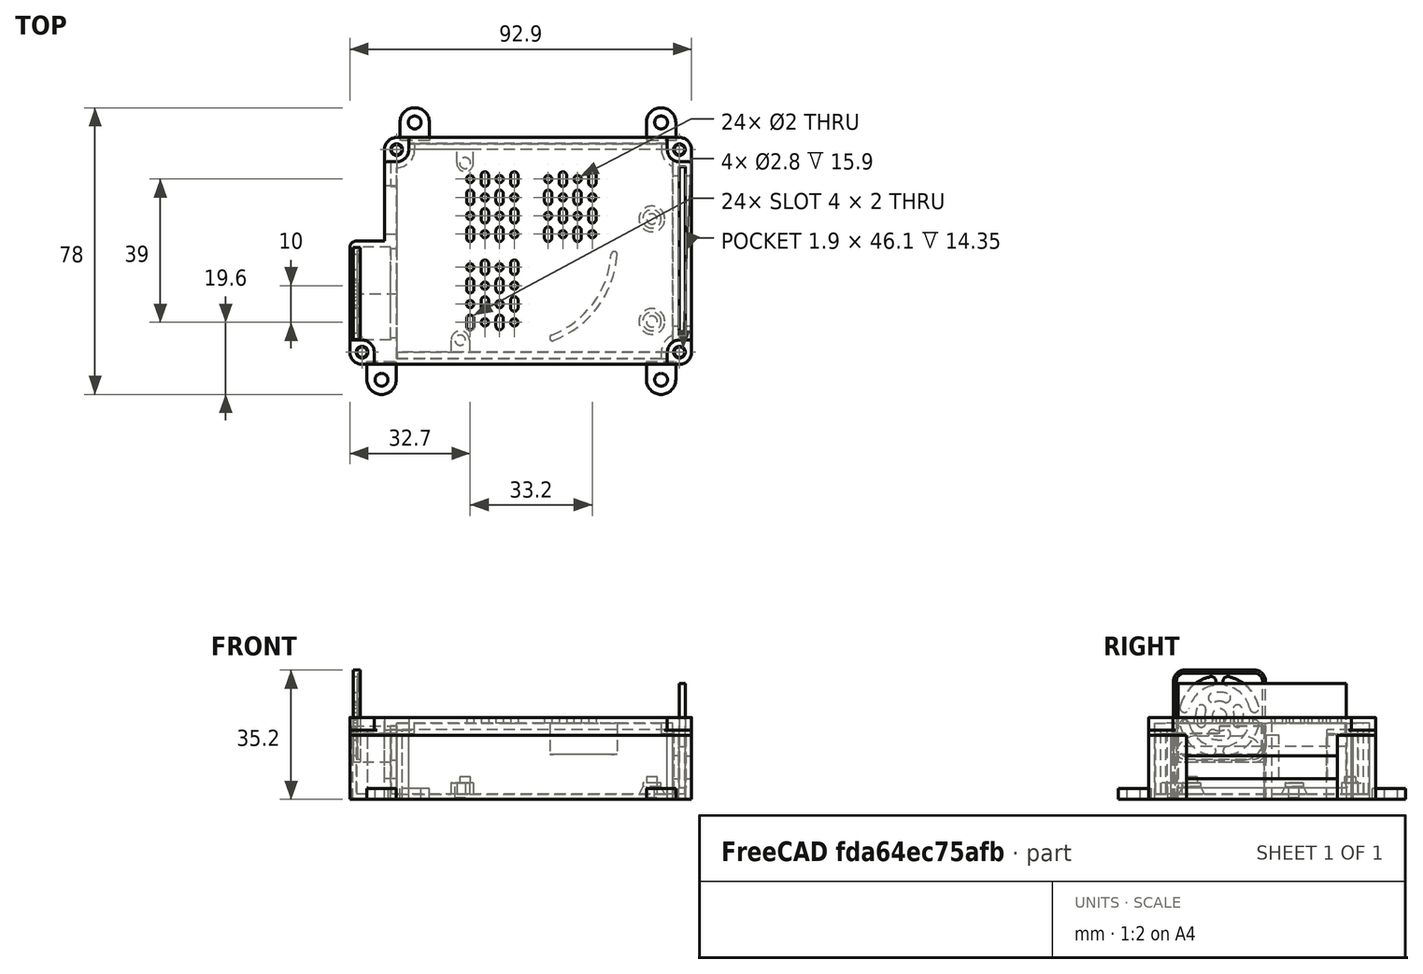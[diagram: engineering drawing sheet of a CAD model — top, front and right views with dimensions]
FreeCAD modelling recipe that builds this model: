
FCSTD DOCUMENT  (FreeCAD 1.0R39319 (Git))
Label: Enclosure
License: All rights reserved
LicenseURL: https://en.wikipedia.org/wiki/All_rights_reserved
objects: Sketcher::SketchObject×31, PartDesign::Pocket×17, PartDesign::Pad×13, PartDesign::Body×9, PartDesign::Fillet×8, PartDesign::FeatureBase×4, App::Part×3, Mesh::Feature×2, PartDesign::PolarPattern×2, Spreadsheet::Sheet×1, PartDesign::Chamfer×1
note: 200 computed .brp shape members not serialized (recipe doc carries the construction recipe); baked Part::Feature solids carry a one-line shape summary decoded from their .brp

FEATURE [Sketcher::SketchObject] Sketch  label="Bottom_base_sketch"
  ArcFitTolerance = 1e-06
  AttachmentSupport = -> [XY_Plane]
  FullyConstrained = true
  MakeInternals = false
  MapMode = 5
  expr: .Constraints.Fan_lower_wall_distance = (Spreadsheet.B1 * 2 + 0.1 mm) * 2
  expr: Constraints[53] = Spreadsheet.B1 * 2
  expr: Constraints[54] = Spreadsheet.B1 * 2
  expr: Constraints[56] = Spreadsheet.B1
  expr: Constraints[57] = Spreadsheet.B1 / 2
  expr: Constraints[58] = Spreadsheet.B1 * 2 + 4 mm
  expr: Constraints[67] = Spreadsheet.B1 + 0.1 mm
  sketch-geometry (20):
    g0: LineSegment [constr] StartX=20 StartY=73.3 StartZ=0 EndX=20 EndY=20 EndZ=0
    g1: LineSegment [constr] StartX=20 StartY=20 StartZ=0 EndX=88.6 EndY=20 EndZ=0
    g2: LineSegment [constr] StartX=86 StartY=73.3 StartZ=0 EndX=20 EndY=73.3 EndZ=0
    g3: LineSegment [constr] StartX=86 StartY=73.3 StartZ=0 EndX=86 EndY=60.5 EndZ=0
    g4: LineSegment [constr] StartX=86 StartY=60.5 StartZ=0 EndX=88.6 EndY=60.5 EndZ=0
    g5: LineSegment [constr] StartX=88.6 StartY=60.5 StartZ=0 EndX=88.6 EndY=20 EndZ=0
    g6: LineSegment [constr] StartX=19 StartY=74.3 StartZ=0 EndX=19 EndY=19 EndZ=0
    g7: LineSegment [constr] StartX=19 StartY=19 StartZ=0 EndX=89.6 EndY=19 EndZ=0
    g8: LineSegment [constr] StartX=89.6 StartY=19 StartZ=0 EndX=89.6 EndY=74.3 EndZ=0
    g9: LineSegment [constr] StartX=89.6 StartY=74.3 StartZ=0 EndX=19 EndY=74.3 EndZ=0
    g10: LineSegment [constr] StartX=4.7 StartY=47.7 StartZ=0 EndX=4.7 EndY=22.4 EndZ=0
    g11: LineSegment [constr] StartX=4.7 StartY=22.4 StartZ=0 EndX=15 EndY=22.4 EndZ=0
    g12: LineSegment [constr] StartX=15 StartY=22.4 StartZ=0 EndX=15 EndY=47.7 EndZ=0
    g13: LineSegment [constr] StartX=15 StartY=47.7 StartZ=0 EndX=4.7 EndY=47.7 EndZ=0
    g14: LineSegment StartX=13.3 StartY=49.3 StartZ=0 EndX=13.3 EndY=77.5 EndZ=0
    g15: LineSegment StartX=13.3 StartY=77.5 StartZ=0 EndX=96.8 EndY=77.5 EndZ=0
    g16: LineSegment StartX=96.8 StartY=77.5 StartZ=0 EndX=96.8 EndY=15.8 EndZ=0
    g17: LineSegment StartX=96.8 StartY=15.8 StartZ=0 EndX=3.9 EndY=15.8 EndZ=0
    g18: LineSegment StartX=3.9 StartY=15.8 StartZ=0 EndX=3.9 EndY=49.3 EndZ=0
    g19: LineSegment StartX=3.9 StartY=49.3 StartZ=0 EndX=13.3 EndY=49.3 EndZ=0
  constraints (68):
    c: Vertical(g0)
    c: Horizontal(g1)
    c: Horizontal(g2)
    c: Distance(g0) = 53.3  'PCB_height'
    c: DistanceY(g-1,g0) = 20  'Offset'
    c: DistanceX(g-2,g0) = 20
    c: Distance(g1) = 68.6
    c: Coincident(g1,g0)
    c: Coincident(g2,g0)
    c: Coincident(g3,g2)
    c: Vertical(g3)
    c: Coincident(g4,g3)
    c: Horizontal(g4)
    c: Coincident(g5,g4)
    c: Coincident(g5,g1)
    c: Vertical(g5)
    c: Distance(g2) = 66  'Short_length'
    c: Distance(g3) = 12.8
    c: Coincident(g6,g7)
    c: Coincident(g7,g8)
    c: Coincident(g8,g9)
    c: Coincident(g9,g6)
    c: Vertical(g6)
    c: Vertical(g8)
    c: Horizontal(g7)
    c: Horizontal(g9)
    c: DistanceX(g6,g0) = 1
    c: DistanceY(g2,g8) = 1
    c: DistanceX(g1,g7) = 1
    c: DistanceY(g6,g0) = 1
    c: Coincident(g10,g11)
    c: Coincident(g11,g12)
    c: Coincident(g12,g13)
    c: Coincident(g13,g10)
    c: Vertical(g10)
    c: Vertical(g12)
    c: Horizontal(g11)
    c: Horizontal(g13)
    c: Distance(g10) = 25.3  'Fan_height'
    c: Distance(g11) = 10.3  'Fan_width'
    c: Distance(g11,g0) = 5  'Fan_board_distance'
    c: Vertical(g14)
    c: Coincident(g15,g14)
    c: Horizontal(g15)
    c: Coincident(g16,g15)
    c: Vertical(g16)
    c: Coincident(g17,g16)
    c: Horizontal(g17)
    c: Coincident(g18,g17)
    c: Vertical(g18)
    c: Coincident(g19,g18)
    c: Coincident(g19,g14)
    c: Horizontal(g19)
    c: Distance(g6,g15) = 3.2
    c: Distance(g7,g17) = 3.2
    c: Distance(g14,g0) = 6.7
    c: Distance(g14,g13) = 1.6
    c: Distance(g18,g10) = 0.8
    c: Distance(g16,g8) = 7.2
    c: DistanceX(g-2,g17) = 3.9  'Outer_leftmost_distance'
    c: DistanceY(g-1,g17) = 15.8  'Outer_downmost_distance'
    c: Distance(g19) = 9.4  'Fan_housing_h_length'
    c: Distance(g17) = 92.9  'Outer_housing_width'
    c: Distance(g18) = 33.5  'Fan_housing_v_length'
    c: Distance(g16) = 61.7  'Outer_housing_height'
    c: Distance(g11,g17) = 6.6  'Fan_lower_wall_distance'
    c: DistanceY(g0,g11) = 2.4  'Fan_board_verical_offset'
    c: Distance(g12,g14) = 1.7
FEATURE [Spreadsheet::Sheet] Spreadsheet
  cells = A1='Wall thickness; B1==1.6 mm; A2='Bottom thickness; B2==1.5 mm; A3='USB connector width; B3==13.1 mm; A4='USB connector edge distance; B4==31.2 mm; A5='Top thickness; B5==1.5 mm
FEATURE [PartDesign::Pad] Pad  label="Bottom_base"
  Direction = (0,0,1)
  Length = 1.5
  Length2 = 10
  Profile = -> Sketch
  ReferenceAxis = -> Sketch [N_Axis]
  Refine = true
  Suppressed = false
  Type = 0
  expr: Length = Spreadsheet.B2
FEATURE [Sketcher::SketchObject] Sketch001  label="Bottom_outer_wall_sketch"
  ArcFitTolerance = 1e-06
  AttachmentSupport = -> [Pad]
  FullyConstrained = true
  MakeInternals = false
  MapMode = 5
  Placement = pos=(0,0,1.5) rot=(0,0,1;0rad)
  expr: .Constraints.Breakout_wall_thickness = Spreadsheet.B1 * 2 + 1.9 mm
  expr: .Constraints.Wall_thickness = Spreadsheet.B1 * 2 + 0.1 mm
  expr: Constraints[12] = <<Bottom_base_sketch>>.Constraints.Outer_leftmost_distance
  expr: Constraints[13] = <<Bottom_base_sketch>>.Constraints.Fan_housing_v_length
  expr: Constraints[14] = <<Bottom_base_sketch>>.Constraints.Outer_downmost_distance
  expr: Constraints[15] = <<Bottom_base_sketch>>.Constraints.Outer_housing_width
  expr: Constraints[16] = <<Bottom_base_sketch>>.Constraints.Outer_housing_height
  expr: Constraints[17] = <<Bottom_base_sketch>>.Constraints.Fan_housing_h_length
  expr: Constraints[18] = .Constraints.Wall_thickness
  expr: Constraints[19] = <<Bottom_base_sketch>>.Constraints.Offset
  expr: Constraints[20] = <<Bottom_base_sketch>>.Constraints.Offset
  expr: Constraints[27] = <<Bottom_base_sketch>>.Constraints.Fan_height
  expr: Constraints[32] = .Constraints.Wall_thickness
  expr: Constraints[37] = .Constraints.Wall_thickness
  expr: Constraints[38] = .Constraints.Wall_thickness
  expr: Constraints[44] = .Constraints.Wall_thickness
  expr: Constraints[59] = <<Bottom_base_sketch>>.Constraints.Fan_board_distance
  expr: Constraints[60] = <<Bottom_base_sketch>>.Constraints.Fan_board_verical_offset
  expr: Constraints[63] = .Constraints.Wall_thickness
  sketch-geometry (19):
    g0: LineSegment StartX=96.8 StartY=77.5 StartZ=0 EndX=13.3 EndY=77.5 EndZ=0
    g1: LineSegment StartX=13.3 StartY=77.5 StartZ=0 EndX=13.3 EndY=49.3 EndZ=0
    g2: LineSegment StartX=13.3 StartY=49.3 StartZ=0 EndX=3.9 EndY=49.3 EndZ=0
    g3: LineSegment StartX=3.9 StartY=49.3 StartZ=0 EndX=3.9 EndY=15.8 EndZ=0
    g4: LineSegment StartX=3.9 StartY=15.8 StartZ=0 EndX=96.8 EndY=15.8 EndZ=0
    g5: LineSegment StartX=96.8 StartY=15.8 StartZ=0 EndX=96.8 EndY=77.5 EndZ=0
    g6: GeomPoint [constr] X=20 Y=20 Z=0
    g7: LineSegment [constr] StartX=4.7 StartY=47.7 StartZ=0 EndX=4.7 EndY=22.4 EndZ=0
    g8: LineSegment [constr] StartX=15 StartY=22.4 StartZ=0 EndX=15 EndY=47.7 EndZ=0
    g9: LineSegment [constr] StartX=15 StartY=47.7 StartZ=0 EndX=4.7 EndY=47.7 EndZ=0
    g10: LineSegment StartX=16.6 StartY=70.9 StartZ=0 EndX=16.6 EndY=19.1 EndZ=0
    g11: ArcOfCircle CenterX=16.6 CenterY=74.2 CenterZ=0 NormalX=0 NormalY=0 NormalZ=1 AngleXU=0 Radius=3.3 StartAngle=4.71239 EndAngle=6.28319
    g12: LineSegment StartX=90.2 StartY=74.2 StartZ=0 EndX=19.9 EndY=74.2 EndZ=0
    g13: ArcOfCircle CenterX=93.5 CenterY=74.2 CenterZ=0 NormalX=0 NormalY=0 NormalZ=1 AngleXU=0 Radius=3.3 StartAngle=3.14159 EndAngle=4.13546
    g14: LineSegment StartX=91.7 StartY=21.8659 StartZ=0 EndX=91.7 EndY=71.4341 EndZ=0
    g15: LineSegment StartX=16.6 StartY=19.1 StartZ=0 EndX=90.2 EndY=19.1 EndZ=0
    g16: ArcOfCircle CenterX=93.5 CenterY=19.1 CenterZ=0 NormalX=0 NormalY=0 NormalZ=1 AngleXU=0 Radius=3.3 StartAngle=2.14773 EndAngle=3.14159
    g17: LineSegment [constr] StartX=4.7 StartY=22.4 StartZ=0 EndX=15 EndY=22.4 EndZ=0
    g18: LineSegment [constr] StartX=93.5 StartY=19.1 StartZ=0 EndX=93.5 EndY=74.2 EndZ=0
  constraints (68):
    c: Horizontal(g0)
    c: Coincident(g1,g0)
    c: Vertical(g1)
    c: Coincident(g2,g1)
    c: Horizontal(g2)
    c: Coincident(g3,g2)
    c: Vertical(g3)
    c: Coincident(g4,g3)
    c: Horizontal(g4)
    c: Coincident(g5,g4)
    c: Coincident(g5,g0)
    c: Vertical(g5)
    c: DistanceX(g-2,g3) = 3.9
    c: Distance(g3) = 33.5
    c: DistanceY(g-1,g3) = 15.8
    c: Distance(g4) = 92.9
    c: Distance(g5) = 61.7
    c: Distance(g2) = 9.4
    c: DistanceY(g3,g15) = 3.3
    c: DistanceX(g-2,g6) = 20
    c: DistanceY(g-1,g6) = 20
    c: Coincident(g7,g17)
    c: Coincident(g8,g9)
    c: Coincident(g9,g7)
    c: Vertical(g7)
    c: Vertical(g8)
    c: Horizontal(g9)
    c: Distance(g7) = 25.3
    c: Vertical(g10)
    c: Distance(g10,g1) = 3.3  'Wall_thickness'
    c: Coincident(g11,g12)
    c: Coincident(g11,g10)
    c: Radius(g11) = 3.3
    c: PointOnObject(g11,g10)
    c: Horizontal(g12)
    c: Coincident(g13,g12)
    c: Coincident(g13,g14)
    c: Radius(g13) = 3.3
    c: Distance(g13,g0) = 3.3
    c: PointOnObject(g11,g12)
    c: Vertical(g14)
    c: Horizontal(g15)
    c: Coincident(g16,g14)
    c: Coincident(g16,g15)
    c: Radius(g16) = 3.3
    c: Distance(g14,g5) = 5.1  'Breakout_wall_thickness'
    c: Distance(g-1,g10) = 16.6  'Left_inner_wall_distance'
    c: Distance(g-1,g15) = 19.1  'Lower_inner_wall_distance'
    c: Distance(g-1,g12) = 74.2  'Upper_inner_wall_distance'
    c: Distance(g12) = 70.3  'Uppoer_pos_pin_length'
    c: Distance(g15) = 73.6  'Lower_pos_pin_length'
    c: Distance(g6,g14) = 71.7  'Breakout_board_distance'
    c: DistanceX(g-2,g11) = 16.6  'Left_hole_h_distance'
    c: DistanceY(g-1,g11) = 74.2  'Upper_hole_h_distance'
    c: DistanceY(g-1,g16) = 19.1  'Lower_hole_h_distance'
    c: DistanceX(g-2,g16) = 93.5  'Right_hole_h_distance'
    c: Horizontal(g17)
    c: Distance(g17,g8) = 10.3
    c: Coincident(g17,g8)
    c: DistanceX(g8,g6) = 5
    c: DistanceY(g6,g8) = 2.4
    c: PointOnObject(g16,g15)
    c: PointOnObject(g13,g12)
    c: Distance(g13,g5) = 3.3
    c: Coincident(g18,g16)
    c: Coincident(g18,g13)
    c: Vertical(g18)
    c: Coincident(g10,g15)
FEATURE [PartDesign::Pad] Pad001  label="Bottom_outer_wall"
  BaseFeature = -> Pad
  Direction = (0,0,1)
  Length = 15.9
  Length2 = 10
  Profile = -> Sketch001
  ReferenceAxis = -> Sketch001 [N_Axis]
  Refine = true
  Suppressed = false
  Type = 0
  expr: Length = 15.9 mm
FEATURE [Mesh::Feature] Fan
  Placement = pos=(4.85,22.55,10.2) rot=(0,0,1;0rad)
  expr: .Placement.Base.z = <<Bottom_base>>.Length + <<Bottom_outer_wall>>.Length - <<Bottom_fan_outer_cut>>.Length - <<Bottom_fan_inner_cut>>.Length + 0.15 mm
FEATURE [Sketcher::SketchObject] Sketch002  label="Bottom_fan_outer_cut_sketch"
  ArcFitTolerance = 1e-06
  AttachmentSupport = -> [Pad001]
  FullyConstrained = true
  MakeInternals = false
  MapMode = 5
  Placement = pos=(0,0,17.4) rot=(0,0,1;0rad)
  expr: Constraints[10] = <<Bottom_base_sketch>>.Constraints.Offset
  expr: Constraints[11] = <<Bottom_base_sketch>>.Constraints.Offset
  expr: Constraints[12] = <<Bottom_base_sketch>>.Constraints.Fan_board_distance
  expr: Constraints[21] = .Constraints.Fan_clamp_length
  expr: Constraints[36] = Spreadsheet.B1 * 2
  expr: Constraints[37] = <<Bottom_base_sketch>>.Constraints.Fan_board_verical_offset
  expr: Constraints[8] = <<Bottom_base_sketch>>.Constraints.Fan_width
  expr: Constraints[9] = Spreadsheet.B1 * 2
  sketch-geometry (13):
    g0: LineSegment StartX=4.7 StartY=22.4 StartZ=0 EndX=15 EndY=22.4 EndZ=0
    g1: LineSegment StartX=15 StartY=22.4 StartZ=0 EndX=15 EndY=22.9 EndZ=0
    g2: LineSegment StartX=15 StartY=22.9 StartZ=0 EndX=18.2 EndY=22.9 EndZ=0
    g3: LineSegment StartX=15 StartY=47.7 StartZ=0 EndX=4.7 EndY=47.7 EndZ=0
    g4: GeomPoint X=20 Y=20 Z=0
    g5: LineSegment StartX=15 StartY=47.7 StartZ=0 EndX=15 EndY=47.2 EndZ=0
    g6: LineSegment StartX=15 StartY=47.2 StartZ=0 EndX=18.2 EndY=47.2 EndZ=0
    g7: LineSegment StartX=18.2 StartY=47.2 StartZ=0 EndX=18.2 EndY=22.9 EndZ=0
    g8: LineSegment StartX=4.7 StartY=47.7 StartZ=0 EndX=4.7 EndY=47.2 EndZ=0
    g9: LineSegment StartX=4.7 StartY=22.9 StartZ=0 EndX=4.7 EndY=22.4 EndZ=0
    g10: LineSegment StartX=4.7 StartY=47.2 StartZ=0 EndX=1.5 EndY=47.2 EndZ=0
    g11: LineSegment StartX=4.7 StartY=22.9 StartZ=0 EndX=1.5 EndY=22.9 EndZ=0
    g12: LineSegment StartX=1.5 StartY=22.9 StartZ=0 EndX=1.5 EndY=47.2 EndZ=0
  constraints (40):
    c: Coincident(g0,g9)
    c: Horizontal(g0)
    c: Coincident(g1,g0)
    c: Vertical(g1)
    c: Coincident(g2,g1)
    c: Horizontal(g2)
    c: Horizontal(g3)
    c: Coincident(g3,g8)
    c: Distance(g0) = 10.3
    c: Distance(g2) = 3.2
    c: DistanceY(g-1,g4) = 20
    c: DistanceX(g-2,g4) = 20
    c: DistanceX(g0,g4) = 5
    c: Coincident(g5,g3)
    c: Vertical(g5)
    c: Coincident(g6,g5)
    c: Horizontal(g6)
    c: Coincident(g7,g6)
    c: Coincident(g7,g2)
    c: Vertical(g7)
    c: Distance(g1) = 0.5  'Fan_clamp_length'
    c: Distance(g5) = 0.5
    c: PointOnObject(g5,g1)
    c: Vertical(g8)
    c: Distance(g8,g9) = 25.3
    c: Vertical(g9)
    c: Coincident(g10,g8)
    c: Horizontal(g10)
    c: Coincident(g11,g9)
    c: Horizontal(g11)
    c: Coincident(g12,g11)
    c: Coincident(g12,g10)
    c: Vertical(g12)
    c: PointOnObject(g8,g6)
    c: PointOnObject(g9,g2)
    c: PointOnObject(g8,g9)
    c: Distance(g10) = 3.2
    c: DistanceY(g4,g0) = 2.4
    c: DistanceX(g-2,g0) = 4.7  'Left_distance'
    c: DistanceY(g-1,g0) = 22.4  'Bottom_distance'
FEATURE [Sketcher::SketchObject] Sketch003  label="Bottom_PCB_spacers_sketch"
  ArcFitTolerance = 1e-06
  AttachmentSupport = -> [Pad001]
  FullyConstrained = true
  MakeInternals = false
  MapMode = 5
  Placement = pos=(0,0,1.5) rot=(0,0,1;0rad)
  expr: .Constraints.Diameter = 5 mm
  expr: Constraints[10] = <<Bottom_base_sketch>>.Constraints.Offset
  expr: Constraints[11] = <<Bottom_base_sketch>>.Constraints.Offset
  expr: Constraints[12] = <<Bottom_base_sketch>>.Constraints.Short_length
  expr: Constraints[1] = .Constraints.Diameter
  expr: Constraints[2] = .Constraints.Diameter
  sketch-geometry (16):
    g0: Circle [constr] CenterX=35.2 CenterY=70.55 CenterZ=0 NormalX=0 NormalY=0 NormalZ=1 AngleXU=0 Radius=2.25
    g1: Circle CenterX=86 CenterY=55.35 CenterZ=0 NormalX=0 NormalY=0 NormalZ=1 AngleXU=0 Radius=2.5
    g2: Circle CenterX=86 CenterY=27.45 CenterZ=0 NormalX=0 NormalY=0 NormalZ=1 AngleXU=0 Radius=2.5
    g3: Circle [constr] CenterX=33.9 CenterY=22.35 CenterZ=0 NormalX=0 NormalY=0 NormalZ=1 AngleXU=0 Radius=2.5
    g4: LineSegment [constr] StartX=86 StartY=55.35 StartZ=0 EndX=86 EndY=27.45 EndZ=0
    g5: GeomPoint [constr] X=20 Y=20 Z=0
    g6: ArcOfCircle CenterX=33.9 CenterY=22.35 CenterZ=0 NormalX=0 NormalY=0 NormalZ=1 AngleXU=0 Radius=2.5 StartAngle=-1.8e-15 EndAngle=3.14159
    g7: LineSegment StartX=31.4 StartY=22.35 StartZ=0 EndX=31.4 EndY=18 EndZ=0
    g8: LineSegment StartX=36.4 StartY=22.35 StartZ=0 EndX=36.4 EndY=18 EndZ=0
    g9: LineSegment StartX=36.4 StartY=18 StartZ=0 EndX=31.4 EndY=18 EndZ=0
    g10: LineSegment [constr] StartX=31.4 StartY=22.35 StartZ=0 EndX=36.4 EndY=22.35 EndZ=0
    g11: ArcOfCircle CenterX=35.2 CenterY=70.55 CenterZ=0 NormalX=0 NormalY=0 NormalZ=1 AngleXU=0 Radius=2.25 StartAngle=3.14159 EndAngle=6.28319
    g12: LineSegment [constr] StartX=32.95 StartY=70.55 StartZ=0 EndX=37.45 EndY=70.55 EndZ=0
    g13: LineSegment StartX=32.95 StartY=70.55 StartZ=0 EndX=32.95 EndY=75.55 EndZ=0
    g14: LineSegment StartX=37.45 StartY=70.55 StartZ=0 EndX=37.45 EndY=75.55 EndZ=0
    g15: LineSegment StartX=32.95 StartY=75.55 StartZ=0 EndX=37.45 EndY=75.55 EndZ=0
  constraints (45):
    c: Diameter(g3) = 5  'Diameter'
    c: Diameter(g2) = 5
    c: Diameter(g1) = 5
    c: Diameter(g0) = 4.5
    c: DistanceY(g3,g2) = 5.1
    c: DistanceY(g1,g0) = 15.2
    c: Coincident(g4,g1)
    c: Coincident(g4,g2)
    c: Vertical(g4)
    c: Distance(g4) = 27.9
    c: DistanceY(g-1,g5) = 20
    c: DistanceX(g-2,g5) = 20
    c: Distance(g5,g4) = 66
    c: DistanceY(g5,g3) = 2.35
    c: DistanceX(g3,g0) = 1.3
    c: DistanceX(g3,g2) = 52.1
    c: DistanceX(g0,g1) = 50.8
    c: Coincident(g6,g3)
    c: Coincident(g7,g6)
    c: Vertical(g7)
    c: Coincident(g8,g6)
    c: Vertical(g8)
    c: Coincident(g9,g8)
    c: Coincident(g9,g7)
    c: Horizontal(g9)
    c: Coincident(g10,g6)
    c: Coincident(g10,g6)
    c: Horizontal(g10)
    c: PointOnObject(g3,g10)
    c: PointOnObject(g6,g3)
    c: Distance(g5,g9) = 2
    c: Coincident(g11,g0)
    c: Coincident(g12,g11)
    c: Coincident(g12,g11)
    c: Horizontal(g12)
    c: Coincident(g13,g11)
    c: Vertical(g13)
    c: Coincident(g14,g11)
    c: Vertical(g14)
    c: Coincident(g15,g13)
    c: Coincident(g15,g14)
    c: Horizontal(g15)
    c: PointOnObject(g0,g12)
    c: PointOnObject(g11,g0)
    c: Distance(g13) = 5
FEATURE [PartDesign::Pad] Pad002  label="Bottom_PCB_spacers"
  BaseFeature = -> Pad001
  Direction = (0,0,1)
  Length = 3
  Length2 = 10
  Profile = -> Sketch003
  ReferenceAxis = -> Sketch003 [N_Axis]
  Refine = true
  Suppressed = false
  Type = 0
FEATURE [Sketcher::SketchObject] Sketch004  label="Bottom_PCB_pins_sketch"
  ArcFitTolerance = 1e-06
  AttachmentSupport = -> [Pad002]
  FullyConstrained = true
  MakeInternals = false
  MapMode = 5
  Placement = pos=(0,0,4.5) rot=(0,0,1;0rad)
  expr: Constraints[12] = <<Bottom_base_sketch>>.Constraints.Offset
  expr: Constraints[13] = <<Bottom_base_sketch>>.Constraints.Offset
  expr: Constraints[14] = <<Bottom_base_sketch>>.Constraints.Short_length
  expr: Constraints[1] = .Constraints.Diameter
  expr: Constraints[2] = .Constraints.Diameter
  expr: Constraints[3] = .Constraints.Diameter
  sketch-geometry (6):
    g0: Circle CenterX=35.2 CenterY=70.55 CenterZ=0 NormalX=0 NormalY=0 NormalZ=1 AngleXU=0 Radius=1.5
    g1: Circle [constr] CenterX=86 CenterY=55.35 CenterZ=0 NormalX=0 NormalY=0 NormalZ=1 AngleXU=0 Radius=1.5
    g2: Circle CenterX=86 CenterY=27.45 CenterZ=0 NormalX=0 NormalY=0 NormalZ=1 AngleXU=0 Radius=1.5
    g3: Circle [constr] CenterX=34.1 CenterY=22.75 CenterZ=0 NormalX=0 NormalY=0 NormalZ=1 AngleXU=0 Radius=1.5
    g4: LineSegment [constr] StartX=86 StartY=55.35 StartZ=0 EndX=86 EndY=27.45 EndZ=0
    g5: GeomPoint [constr] X=20 Y=20 Z=0
  constraints (16):
    c: Diameter(g3) = 3  'Diameter'
    c: Diameter(g2) = 3
    c: Diameter(g1) = 3
    c: Diameter(g0) = 3
    c: DistanceX(g0,g1) = 50.8
    c: DistanceY(g1,g0) = 15.2
    c: Coincident(g4,g1)
    c: Coincident(g4,g2)
    c: Vertical(g4)
    c: Distance(g4) = 27.9
    c: DistanceY(g3,g2) = 4.7
    c: DistanceX(g3,g0) = 1.1
    c: DistanceY(g-1,g5) = 20
    c: DistanceX(g-2,g5) = 20
    c: Distance(g5,g4) = 66
    c: DistanceY(g5,g3) = 2.75
FEATURE [PartDesign::Pad] Pad003  label="Bottom_PCB_pins"
  BaseFeature = -> Pad002
  Direction = (0,0,1)
  Length = 1.6
  Length2 = 10
  Profile = -> Sketch004
  ReferenceAxis = -> Sketch004 [N_Axis]
  Refine = true
  Suppressed = false
  Type = 0
FEATURE [Sketcher::SketchObject] Sketch005  label="Bottom_position_pins_sketch"
  ArcFitTolerance = 1e-06
  AttachmentSupport = -> [Pad003]
  FullyConstrained = true
  MakeInternals = false
  MapMode = 5
  Placement = pos=(0,0,17.4) rot=(0,0,1;0rad)
  expr: .Constraints.Wall_thickness = Spreadsheet.B1
  expr: Constraints[17] = .Constraints.Wall_thickness
  expr: Constraints[18] = .Constraints.Wall_thickness
  expr: Constraints[19] = <<Bottom_outer_wall_sketch>>.Constraints.Left_inner_wall_distance
  expr: Constraints[20] = <<Bottom_outer_wall_sketch>>.Constraints.Upper_inner_wall_distance
  expr: Constraints[22] = <<Bottom_outer_wall_sketch>>.Constraints.Wall_thickness
  expr: Constraints[23] = <<Bottom_outer_wall_sketch>>.Constraints.Lower_inner_wall_distance
  expr: Constraints[56] = <<Bottom_outer_wall_sketch>>.Constraints.Uppoer_pos_pin_length - 0.2 mm
  sketch-geometry (20):
    g0: LineSegment StartX=90.1 StartY=75.8 StartZ=0 EndX=90.1 EndY=74.2 EndZ=0
    g1: LineSegment StartX=16.6 StartY=58.9 StartZ=0 EndX=15 EndY=58.9 EndZ=0
    g2: LineSegment [constr] StartX=19.9 StartY=75.8 StartZ=0 EndX=19.9 EndY=74.2 EndZ=0
    g3: LineSegment [constr] StartX=15 StartY=70.9 StartZ=0 EndX=16.6 EndY=70.9 EndZ=0
    g4: LineSegment [constr] StartX=16.6 StartY=19.1 StartZ=0 EndX=16.6 EndY=17.5 EndZ=0
    g5: LineSegment StartX=90.1 StartY=17.5 StartZ=0 EndX=90.1 EndY=19.1 EndZ=0
    g6: ArcOfCircle [constr] CenterX=16.6 CenterY=74.2 CenterZ=0 NormalX=0 NormalY=0 NormalZ=1 AngleXU=0 Radius=3.3 StartAngle=4.71239 EndAngle=6.28319
    g7: LineSegment StartX=20 StartY=75.8 StartZ=0 EndX=90.1 EndY=75.8 EndZ=0
    g8: LineSegment StartX=90.1 StartY=74.2 StartZ=0 EndX=20 EndY=74.2 EndZ=0
    g9: LineSegment StartX=20 StartY=75.8 StartZ=0 EndX=20 EndY=74.2 EndZ=0
    g10: LineSegment [constr] StartX=15 StartY=70.9 StartZ=0 EndX=15 EndY=70.8 EndZ=0
    g11: LineSegment StartX=15 StartY=70.8 StartZ=0 EndX=15 EndY=58.9 EndZ=0
    g12: LineSegment [constr] StartX=16.6 StartY=70.9 StartZ=0 EndX=16.6 EndY=70.8 EndZ=0
    g13: LineSegment StartX=16.6 StartY=70.8 StartZ=0 EndX=16.6 EndY=58.9 EndZ=0
    g14: LineSegment StartX=15 StartY=70.8 StartZ=0 EndX=16.6 EndY=70.8 EndZ=0
    g15: LineSegment StartX=90.1 StartY=19.1 StartZ=0 EndX=16.7 EndY=19.1 EndZ=0
    g16: LineSegment [constr] StartX=16.7 StartY=19.1 StartZ=0 EndX=16.6 EndY=19.1 EndZ=0
    g17: LineSegment [constr] StartX=16.6 StartY=17.5 StartZ=0 EndX=16.7 EndY=17.5 EndZ=0
    g18: LineSegment StartX=16.7 StartY=17.5 StartZ=0 EndX=90.1 EndY=17.5 EndZ=0
    g19: LineSegment StartX=16.7 StartY=19.1 StartZ=0 EndX=16.7 EndY=17.5 EndZ=0
  constraints (59):
    c: Coincident(g0,g7)
    c: Vertical(g0)
    c: Coincident(g8,g0)
    c: Coincident(g1,g13)
    c: Horizontal(g1)
    c: Coincident(g11,g1)
    c: Coincident(g3,g10)
    c: Coincident(g3,g12)
    c: Vertical(g2)
    c: Horizontal(g3)
    c: Vertical(g4)
    c: Coincident(g17,g4)
    c: Coincident(g5,g18)
    c: Coincident(g15,g5)
    c: Coincident(g16,g4)
    c: Vertical(g5)
    c: Distance(g3) = 1.6  'Wall_thickness'
    c: Distance(g2) = 1.6
    c: Distance(g4) = 1.6
    c: DistanceX(g-2,g1) = 16.6
    c: DistanceY(g-1,g2) = 74.2
    c: Coincident(g6,g12)
    c: Radius(g6) = 3.3
    c: DistanceY(g-1,g4) = 19.1
    c: Horizontal(g7)
    c: Horizontal(g8)
    c: PointOnObject(g6,g8)
    c: Coincident(g9,g7)
    c: Coincident(g9,g8)
    c: Vertical(g9)
    c: PointOnObject(g2,g8)
    c: PointOnObject(g2,g7)
    c: Coincident(g2,g6)
    c: Coincident(g10,g11)
    c: Vertical(g10)
    c: Vertical(g11)
    c: Coincident(g12,g13)
    c: Vertical(g12)
    c: Vertical(g13)
    c: PointOnObject(g6,g12)
    c: Distance(g12,g13) = 12
    c: Coincident(g14,g10)
    c: Coincident(g14,g12)
    c: Horizontal(g14)
    c: Distance(g10) = 0.1
    c: Coincident(g15,g16)
    c: Horizontal(g15)
    c: Horizontal(g16)
    c: Coincident(g17,g18)
    c: Horizontal(g17)
    c: Horizontal(g18)
    c: Coincident(g19,g15)
    c: Coincident(g19,g17)
    c: Vertical(g19)
    c: Distance(g16) = 0.1
    c: PointOnObject(g5,g0)
    c: Distance(g8) = 70.1
    c: PointOnObject(g4,g13)
    c: Distance(g7,g2) = 0.1
FEATURE [PartDesign::Pad] Pad004  label="Bottom_position_pins"
  BaseFeature = -> Pad003
  Direction = (0,0,1)
  Length = 1.6
  Length2 = 10
  Profile = -> Sketch005
  ReferenceAxis = -> Sketch005 [N_Axis]
  Refine = true
  Suppressed = false
  Type = 0
  expr: Length = Spreadsheet.B1
FEATURE [Sketcher::SketchObject] Sketch006  label="Breakout_sketch"
  ArcFitTolerance = 1e-06
  AttachmentSupport = -> [YZ_Plane001]
  FullyConstrained = true
  MakeInternals = false
  MapMode = 5
  Placement = pos=(0,0,0) rot=(0.57735,0.57735,0.57735;2.0944rad)
  sketch-geometry (4):
    g0: LineSegment StartX=0 StartY=0 StartZ=0 EndX=45.8 EndY=0 EndZ=0
    g1: LineSegment StartX=45.8 StartY=0 StartZ=0 EndX=45.8 EndY=28.4 EndZ=0
    g2: LineSegment StartX=45.8 StartY=28.4 StartZ=0 EndX=0 EndY=28.4 EndZ=0
    g3: LineSegment StartX=0 StartY=28.4 StartZ=0 EndX=0 EndY=0 EndZ=0
  constraints (11):
    c: Coincident(g0,g1)
    c: Coincident(g1,g2)
    c: Coincident(g2,g3)
    c: Coincident(g3,g0)
    c: Horizontal(g0)
    c: Horizontal(g2)
    c: Vertical(g1)
    c: Vertical(g3)
    c: Coincident(g0,g-1)
    c: Distance(g2) = 45.8  'Width'
    c: Distance(g3) = 28.4  'Height'
FEATURE [PartDesign::Pad] Pad005
  Direction = (1,0,0)
  Length = 1.6
  Length2 = 10
  Placement = pos=(0,0,0) rot=(1,1,1;2.0944rad)
  Profile = -> Sketch006
  ReferenceAxis = -> Sketch006 [N_Axis]
  Refine = true
  Suppressed = false
  Type = 0
FEATURE [PartDesign::Body] Body001  label="Breakout"
  AllowCompound = false
  Group = -> [Sketch006,Pad005]
  Origin = -> Origin001
  Placement = pos=(93.45,23.75,3.2) rot=(0,0,1;0rad)
  Tip = -> Pad005
  expr: .Placement.Base.z = <<Bottom_base>>.Length + <<Bottom_outer_wall>>.Length - <<Bottom_breakout_slot>>.Length + 0.15 mm
FEATURE [Sketcher::SketchObject] Sketch007  label="Bottom_breakout_slot_sketch"
  ArcFitTolerance = 1e-06
  AttachmentSupport = -> [Pad004]
  FullyConstrained = true
  MakeInternals = false
  MapMode = 5
  Placement = pos=(0,0,17.4) rot=(0,0,1;0rad)
  expr: .Constraints.Slot_height = <<Breakout_sketch>>.Constraints.Width + 0.3 mm
  expr: .Constraints.Vertical_center_distance = <<Bottom_base_sketch>>.Constraints.PCB_height / 2
  expr: Constraints[10] = <<Bottom_base_sketch>>.Constraints.Offset
  expr: Constraints[11] = <<Bottom_base_sketch>>.Constraints.Offset
  expr: Constraints[12] = <<Bottom_outer_wall_sketch>>.Constraints.Breakout_board_distance + Spreadsheet.B1
  sketch-geometry (8):
    g0: LineSegment StartX=93.3 StartY=23.6 StartZ=0 EndX=93.3 EndY=69.7 EndZ=0
    g1: LineSegment StartX=93.3 StartY=69.7 StartZ=0 EndX=95.2 EndY=69.7 EndZ=0
    g2: LineSegment StartX=95.2 StartY=69.7 StartZ=0 EndX=95.2 EndY=23.6 EndZ=0
    g3: LineSegment StartX=95.2 StartY=23.6 StartZ=0 EndX=93.3 EndY=23.6 EndZ=0
    g4: GeomPoint X=20 Y=20 Z=0
    g5: LineSegment [constr] StartX=95.2 StartY=69.7 StartZ=0 EndX=93.3 EndY=23.6 EndZ=0
    g6: LineSegment [constr] StartX=95.2 StartY=23.6 StartZ=0 EndX=93.3 EndY=69.7 EndZ=0
    g7: GeomPoint [constr] X=94.25 Y=46.65 Z=0
  constraints (21):
    c: Vertical(g0)
    c: Coincident(g1,g0)
    c: Horizontal(g1)
    c: Coincident(g2,g1)
    c: Vertical(g2)
    c: Horizontal(g3)
    c: Distance(g3) = 1.9  'Slot_width'
    c: DistanceY(g3,g0) = 46.1  'Slot_height'
    c: Coincident(g3,g0)
    c: Coincident(g2,g3)
    c: DistanceY(g-1,g4) = 20
    c: DistanceX(g-2,g4) = 20
    c: Distance(g4,g0) = 73.3
    c: Coincident(g5,g1)
    c: Coincident(g5,g0)
    c: Coincident(g6,g2)
    c: Coincident(g6,g0)
    c: PointOnObject(g7,g5)
    c: PointOnObject(g7,g6)
    c: DistanceY(g4,g7) = 26.65  'Vertical_center_distance'
    c: DistanceX(g4,g7) = 74.25  'Horizontal_center_distance'
FEATURE [PartDesign::Pocket] Pocket001  label="Bottom_breakout_slot"
  BaseFeature = -> Pad004
  Direction = (0,0,-1)
  Length = 14.35
  Length2 = 5
  Profile = -> Sketch007
  ReferenceAxis = -> Sketch007 [N_Axis]
  Refine = true
  Suppressed = false
  Type = 0
  expr: Length = <<Breakout_sketch>>.Constraints.Height / 2 + 0.15 mm
FEATURE [Sketcher::SketchObject] Sketch008  label="Bottom_breakout_slot_cutout_sketch"
  ArcFitTolerance = 1e-06
  AttachmentSupport = -> [Pocket001]
  FullyConstrained = true
  MakeInternals = false
  MapMode = 5
  Placement = pos=(0,0,17.4) rot=(0,0,1;0rad)
  expr: .Constraints.Height = <<Bottom_breakout_slot_sketch>>.Constraints.Slot_height - 5.08 mm
  expr: Constraints[15] = <<Bottom_base_sketch>>.Constraints.Offset
  expr: Constraints[16] = <<Bottom_base_sketch>>.Constraints.Offset
  expr: Constraints[17] = <<Bottom_breakout_slot_sketch>>.Constraints.Horizontal_center_distance
  expr: Constraints[18] = <<Bottom_breakout_slot_sketch>>.Constraints.Vertical_center_distance
  expr: Constraints[19] = Spreadsheet.B1 * 2.5 + 1.6 mm
  sketch-geometry (8):
    g0: LineSegment StartX=91.45 StartY=67.16 StartZ=0 EndX=91.45 EndY=26.14 EndZ=0
    g1: LineSegment StartX=91.45 StartY=26.14 StartZ=0 EndX=97.05 EndY=26.14 EndZ=0
    g2: LineSegment StartX=97.05 StartY=26.14 StartZ=0 EndX=97.05 EndY=67.16 EndZ=0
    g3: LineSegment StartX=97.05 StartY=67.16 StartZ=0 EndX=91.45 EndY=67.16 EndZ=0
    g4: LineSegment [constr] StartX=91.45 StartY=26.14 StartZ=0 EndX=97.05 EndY=67.16 EndZ=0
    g5: LineSegment [constr] StartX=91.45 StartY=67.16 StartZ=0 EndX=97.05 EndY=26.14 EndZ=0
    g6: GeomPoint [constr] X=94.25 Y=46.65 Z=0
    g7: GeomPoint [constr] X=20 Y=20 Z=0
  constraints (20):
    c: Coincident(g0,g1)
    c: Coincident(g1,g2)
    c: Coincident(g2,g3)
    c: Coincident(g3,g0)
    c: Vertical(g0)
    c: Vertical(g2)
    c: Horizontal(g1)
    c: Horizontal(g3)
    c: Distance(g0) = 41.02  'Height'
    c: Coincident(g4,g0)
    c: Coincident(g4,g2)
    c: Coincident(g5,g0)
    c: Coincident(g5,g1)
    c: PointOnObject(g6,g5)
    c: PointOnObject(g6,g4)
    c: DistanceX(g-2,g7) = 20
    c: DistanceY(g-1,g7) = 20
    c: DistanceX(g7,g6) = 74.25
    c: DistanceY(g7,g6) = 26.65
    c: Distance(g3) = 5.6
FEATURE [PartDesign::Pocket] Pocket002  label="Bottom_breakout_slot_cutout"
  BaseFeature = -> Pocket001
  Direction = (0,0,-1)
  Length = 11.81
  Length2 = 5
  Profile = -> Sketch008
  ReferenceAxis = -> Sketch008 [N_Axis]
  Refine = true
  Suppressed = false
  Type = 0
  expr: Length = <<Bottom_breakout_slot>>.Length - 2.54 mm
FEATURE [Sketcher::SketchObject] Sketch009  label="Bottom_usb_cutout_sketch"
  ArcFitTolerance = 1e-06
  AttachmentSupport = -> [Pocket002]
  FullyConstrained = true
  MakeInternals = false
  MapMode = 5
  Placement = pos=(0,0,19) rot=(0,0,1;0rad)
  expr: Constraints[10] = <<Bottom_base_sketch>>.Constraints.Offset
  expr: Constraints[11] = Spreadsheet.B4
  expr: Constraints[12] = Spreadsheet.B3
  expr: Constraints[8] = Spreadsheet.B1 * 3
  expr: Constraints[9] = <<Bottom_base_sketch>>.Constraints.Offset
  sketch-geometry (5):
    g0: LineSegment StartX=12.2 StartY=64.3 StartZ=0 EndX=12.2 EndY=51.2 EndZ=0
    g1: LineSegment StartX=12.2 StartY=51.2 StartZ=0 EndX=17 EndY=51.2 EndZ=0
    g2: LineSegment StartX=17 StartY=51.2 StartZ=0 EndX=17 EndY=64.3 EndZ=0
    g3: LineSegment StartX=17 StartY=64.3 StartZ=0 EndX=12.2 EndY=64.3 EndZ=0
    g4: GeomPoint X=20 Y=20 Z=0
  constraints (14):
    c: Coincident(g0,g1)
    c: Coincident(g1,g2)
    c: Coincident(g2,g3)
    c: Coincident(g3,g0)
    c: Vertical(g0)
    c: Vertical(g2)
    c: Horizontal(g1)
    c: Horizontal(g3)
    c: Distance(g3) = 4.8
    c: DistanceX(g-2,g4) = 20
    c: DistanceY(g-1,g4) = 20
    c: Distance(g4,g1) = 31.2
    c: Distance(g2) = 13.1
    c: Distance(g4,g2) = 3
FEATURE [PartDesign::Pocket] Pocket003  label="Bottom_usb_cutout"
  BaseFeature = -> Pocket002
  Direction = (0,0,-1)
  Length = 13.2
  Length2 = 5
  Profile = -> Sketch009
  ReferenceAxis = -> Sketch009 [N_Axis]
  Refine = true
  Suppressed = false
  Type = 0
  expr: Length = 13.2 mm
FEATURE [Sketcher::SketchObject] Sketch010  label="Bottom_screw_tunnels_sketch"
  ArcFitTolerance = 1e-06
  AttachmentSupport = -> [Pocket003]
  FullyConstrained = true
  MakeInternals = false
  MapMode = 5
  Placement = pos=(0,0,17.4) rot=(0,0,1;0rad)
  expr: .Constraints.Bottom_distance = <<Bottom_outer_wall_sketch>>.Constraints.Lower_hole_h_distance
  expr: .Constraints.Left_long_distance = <<Bottom_outer_wall_sketch>>.Constraints.Left_hole_h_distance
  expr: .Constraints.Left_short_distance = <<Bottom_base_sketch>>.Constraints.Outer_leftmost_distance + Spreadsheet.B1 * 2 + 0.1 mm
  expr: .Constraints.Lower_horizontal_distance = <<Bottom_outer_wall_sketch>>.Constraints.Right_hole_h_distance
  expr: .Constraints.Vertical_distance = <<Bottom_outer_wall_sketch>>.Constraints.Upper_hole_h_distance
  expr: Constraints[13] = .Constraints.Diameter
  expr: Constraints[1] = .Constraints.Diameter
  expr: Constraints[2] = .Constraints.Diameter
  sketch-geometry (7):
    g0: Circle CenterX=16.6 CenterY=74.2 CenterZ=0 NormalX=0 NormalY=0 NormalZ=1 AngleXU=0 Radius=1.4
    g1: Circle CenterX=93.5 CenterY=74.2 CenterZ=0 NormalX=0 NormalY=0 NormalZ=1 AngleXU=0 Radius=1.4
    g2: Circle CenterX=93.5 CenterY=19.1 CenterZ=0 NormalX=0 NormalY=0 NormalZ=1 AngleXU=0 Radius=1.4
    g3: LineSegment [constr] StartX=16.6 StartY=74.2 StartZ=0 EndX=93.5 EndY=74.2 EndZ=0
    g4: LineSegment [constr] StartX=93.5 StartY=74.2 StartZ=0 EndX=93.5 EndY=19.1 EndZ=0
    g5: Circle CenterX=7.2 CenterY=19.1 CenterZ=0 NormalX=0 NormalY=0 NormalZ=1 AngleXU=0 Radius=1.4
    g6: LineSegment [constr] StartX=7.2 StartY=19.1 StartZ=0 EndX=93.5 EndY=19.1 EndZ=0
  constraints (19):
    c: Diameter(g0) = 2.8  'Diameter'
    c: Diameter(g1) = 2.8
    c: Diameter(g2) = 2.8
    c: Coincident(g3,g0)
    c: Coincident(g3,g1)
    c: Horizontal(g3)
    c: Coincident(g4,g1)
    c: Coincident(g4,g2)
    c: Vertical(g4)
    c: DistanceY(g-1,g0) = 74.2  'Vertical_distance'
    c: DistanceX(g-2,g0) = 16.6  'Left_long_distance'
    c: DistanceY(g-1,g2) = 19.1  'Bottom_distance'
    c: DistanceX(g-2,g2) = 93.5  'Lower_horizontal_distance'
    c: Diameter(g5) = 2.8
    c: Coincident(g6,g5)
    c: Coincident(g6,g2)
    c: Horizontal(g6)
    c: DistanceX(g-2,g5) = 7.2  'Left_short_distance'
    c: Distance(g3) = 76.9  'Top_hole_distance'
FEATURE [PartDesign::Pocket] Pocket004  label="Bottom_screw_tunnels"
  BaseFeature = -> Pocket003
  Direction = (0,0,-1)
  Length = 15.9
  Length2 = 5
  Profile = -> Sketch010
  ReferenceAxis = -> Sketch010 [N_Axis]
  Refine = true
  Suppressed = false
  Type = 0
  expr: Length = <<Bottom_outer_wall>>.Length
FEATURE [Sketcher::SketchObject] Sketch011  label="Top_wall_sketch"
  ArcFitTolerance = 1e-06
  AttachmentSupport = -> [XY_Plane003]
  FullyConstrained = true
  MakeInternals = false
  MapMode = 5
  expr: .Constraints.Pin_thickness = .Constraints.Wall_thickness + 0.1 mm
  expr: .Constraints.Radius = <<Bottom_outer_wall_sketch>>.Constraints.Wall_thickness
  expr: .Constraints.Wall_thickness = Spreadsheet.B1
  expr: Constraints[37] = <<Bottom_base_sketch>>.Constraints.Outer_leftmost_distance
  expr: Constraints[38] = <<Bottom_base_sketch>>.Constraints.Fan_housing_h_length
  expr: Constraints[40] = <<Bottom_base_sketch>>.Constraints.Outer_downmost_distance
  expr: Constraints[41] = <<Bottom_base_sketch>>.Constraints.Outer_housing_width
  expr: Constraints[42] = <<Bottom_base_sketch>>.Constraints.Outer_housing_height
  expr: Constraints[43] = <<Bottom_base_sketch>>.Constraints.Fan_housing_v_length
  expr: Constraints[45] = .Constraints.Wall_thickness
  expr: Constraints[48] = .Constraints.Wall_thickness
  expr: Constraints[49] = .Constraints.Radius
  expr: Constraints[50] = .Constraints.Radius
  expr: Constraints[51] = .Constraints.Pin_thickness
  expr: Constraints[52] = <<Bottom_outer_wall_sketch>>.Constraints.Wall_thickness
  expr: Constraints[59] = <<Bottom_outer_wall_sketch>>.Constraints.Wall_thickness
  expr: Constraints[60] = 6.7 mm
  expr: Constraints[68] = <<Bottom_outer_wall_sketch>>.Constraints.Lower_pos_pin_length
  expr: Constraints[69] = <<Bottom_outer_wall_sketch>>.Constraints.Breakout_wall_thickness
  sketch-geometry (24):
    g0: LineSegment StartX=13.3 StartY=49.3 StartZ=0 EndX=13.3 EndY=77.5 EndZ=0
    g1: LineSegment StartX=13.3 StartY=77.5 StartZ=0 EndX=96.8 EndY=77.5 EndZ=0
    g2: LineSegment StartX=96.8 StartY=77.5 StartZ=0 EndX=96.8 EndY=15.8 EndZ=0
    g3: LineSegment StartX=96.8 StartY=15.8 StartZ=0 EndX=3.9 EndY=15.8 EndZ=0
    g4: LineSegment StartX=3.9 StartY=15.8 StartZ=0 EndX=3.9 EndY=49.3 EndZ=0
    g5: LineSegment StartX=3.9 StartY=49.3 StartZ=0 EndX=13.3 EndY=49.3 EndZ=0
    g6: LineSegment StartX=16.6 StartY=17.4 StartZ=0 EndX=90.2 EndY=17.4 EndZ=0
    g7: LineSegment StartX=90.2 StartY=17.4 StartZ=0 EndX=90.2 EndY=19.1 EndZ=0
    g8: LineSegment StartX=90.2 StartY=74.2 StartZ=0 EndX=90.2 EndY=75.9 EndZ=0
    g9: LineSegment StartX=90.2 StartY=75.9 StartZ=0 EndX=19.9 EndY=75.9 EndZ=0
    g10: LineSegment StartX=19.9 StartY=75.9 StartZ=0 EndX=19.9 EndY=74.2 EndZ=0
    g11: LineSegment StartX=14.9 StartY=70.9 StartZ=0 EndX=16.6 EndY=70.9 EndZ=0
    g12: ArcOfCircle CenterX=16.6 CenterY=74.2 CenterZ=0 NormalX=0 NormalY=0 NormalZ=1 AngleXU=0 Radius=3.3 StartAngle=4.71239 EndAngle=6.28319
    g13: ArcOfCircle CenterX=93.5 CenterY=19.1 CenterZ=0 NormalX=0 NormalY=0 NormalZ=1 AngleXU=0 Radius=3.3 StartAngle=2.14773 EndAngle=3.14159
    g14: ArcOfCircle CenterX=93.5 CenterY=74.2 CenterZ=0 NormalX=0 NormalY=0 NormalZ=1 AngleXU=0 Radius=3.3 StartAngle=3.14159 EndAngle=4.13546
    g15: LineSegment [constr] StartX=16.6 StartY=74.2 StartZ=0 EndX=16.6 EndY=70.9 EndZ=0
    g16: LineSegment [constr] StartX=16.6 StartY=74.2 StartZ=0 EndX=19.9 EndY=74.2 EndZ=0
    g17: LineSegment [constr] StartX=90.2 StartY=74.2 StartZ=0 EndX=93.5 EndY=74.2 EndZ=0
    g18: LineSegment [constr] StartX=93.5 StartY=19.1 StartZ=0 EndX=90.2 EndY=19.1 EndZ=0
    g19: LineSegment StartX=14.9 StartY=70.9 StartZ=0 EndX=14.9 EndY=64.2 EndZ=0
    g20: LineSegment StartX=14.9 StartY=64.2 StartZ=0 EndX=16.6 EndY=64.2 EndZ=0
    g21: LineSegment StartX=16.6 StartY=64.2 StartZ=0 EndX=16.6 EndY=17.4 EndZ=0
    g22: LineSegment StartX=91.7 StartY=71.4341 StartZ=0 EndX=91.7 EndY=21.8659 EndZ=0
    g23: LineSegment [constr] StartX=93.5 StartY=74.2 StartZ=0 EndX=93.5 EndY=19.1 EndZ=0
  constraints (70):
    c: Vertical(g0)
    c: Coincident(g1,g0)
    c: Horizontal(g1)
    c: Coincident(g2,g1)
    c: Vertical(g2)
    c: Coincident(g3,g2)
    c: Horizontal(g3)
    c: Coincident(g4,g3)
    c: Vertical(g4)
    c: Coincident(g5,g4)
    c: Coincident(g5,g0)
    c: Horizontal(g5)
    c: Horizontal(g6)
    c: Coincident(g7,g6)
    c: Vertical(g7)
    c: Vertical(g8)
    c: Coincident(g9,g8)
    c: Horizontal(g9)
    c: Coincident(g10,g9)
    c: Vertical(g10)
    c: Horizontal(g11)
    c: Coincident(g12,g11)
    c: Coincident(g12,g10)
    c: Coincident(g13,g7)
    c: Coincident(g14,g8)
    c: Coincident(g15,g12)
    c: Coincident(g15,g11)
    c: Vertical(g15)
    c: Coincident(g16,g12)
    c: Coincident(g16,g10)
    c: Coincident(g17,g8)
    c: Coincident(g17,g14)
    c: Horizontal(g17)
    c: Coincident(g18,g13)
    c: Coincident(g18,g7)
    c: Horizontal(g18)
    c: Horizontal(g16)
    c: Distance(g-1,g4) = 3.9
    c: Distance(g5) = 9.4
    c: PointOnObject(g8,g16)
    c: Distance(g-1,g3) = 15.8
    c: Distance(g3) = 92.9
    c: Distance(g2) = 61.7
    c: Distance(g4) = 33.5
    c: Distance(g11,g0) = 1.6  'Wall_thickness'
    c: Distance(g9,g1) = 1.6
    c: Radius(g12) = 3.3  'Radius'
    c: Distance(g10) = 1.7  'Pin_thickness'
    c: Distance(g6,g3) = 1.6
    c: Radius(g13) = 3.3
    c: Radius(g14) = 3.3
    c: Distance(g7) = 1.7
    c: Distance(g11,g0) = 3.3
    c: Coincident(g19,g11)
    c: Vertical(g19)
    c: Coincident(g20,g19)
    c: Horizontal(g20)
    c: Coincident(g21,g20)
    c: Vertical(g21)
    c: Distance(g20,g0) = 3.3
    c: Distance(g19) = 6.7
    c: Coincident(g21,g6)
    c: Coincident(g22,g14)
    c: Coincident(g22,g13)
    c: Vertical(g22)
    c: Coincident(g23,g14)
    c: Coincident(g23,g13)
    c: Vertical(g23)
    c: Distance(g6) = 73.6
    c: Distance(g13,g2) = 5.1
FEATURE [PartDesign::Pad] Pad006  label="Top_wall"
  Direction = (0,0,1)
  Length = 17.8
  Length2 = 10
  Profile = -> Sketch011
  ReferenceAxis = -> Sketch011 [N_Axis]
  Refine = true
  Suppressed = false
  Type = 0
FEATURE [PartDesign::Pocket] Pocket  label="Bottom_fan_outer_cut"
  BaseFeature = -> Pocket004
  Direction = (0,0,-1)
  Length = 6.7
  Length2 = 5
  Profile = -> Sketch002
  ReferenceAxis = -> Sketch002 [N_Axis]
  Refine = true
  Suppressed = false
  Type = 0
FEATURE [Sketcher::SketchObject] Sketch014  label="Bottom_fan_inner_cut_sketch"
  ArcFitTolerance = 1e-06
  AttachmentSupport = -> [Pocket]
  FullyConstrained = true
  MakeInternals = false
  MapMode = 5
  Placement = pos=(0,0,10.7) rot=(0,0,1;0rad)
  expr: Constraints[10] = <<Bottom_fan_outer_cut_sketch>>.Constraints.Left_distance
  expr: Constraints[11] = <<Bottom_fan_outer_cut_sketch>>.Constraints.Bottom_distance
  expr: Constraints[8] = <<Bottom_base_sketch>>.Constraints.Fan_height
  expr: Constraints[9] = <<Bottom_base_sketch>>.Constraints.Fan_width
  sketch-geometry (4):
    g0: LineSegment StartX=4.7 StartY=47.7 StartZ=0 EndX=4.7 EndY=22.4 EndZ=0
    g1: LineSegment StartX=4.7 StartY=22.4 StartZ=0 EndX=15 EndY=22.4 EndZ=0
    g2: LineSegment StartX=15 StartY=22.4 StartZ=0 EndX=15 EndY=47.7 EndZ=0
    g3: LineSegment StartX=15 StartY=47.7 StartZ=0 EndX=4.7 EndY=47.7 EndZ=0
  constraints (12):
    c: Coincident(g0,g1)
    c: Coincident(g1,g2)
    c: Coincident(g2,g3)
    c: Coincident(g3,g0)
    c: Vertical(g0)
    c: Vertical(g2)
    c: Horizontal(g1)
    c: Horizontal(g3)
    c: Distance(g0) = 25.3
    c: Distance(g1) = 10.3
    c: Distance(g-1,g0) = 4.7
    c: Distance(g-1,g1) = 22.4
FEATURE [PartDesign::Pocket] Pocket006  label="Bottom_fan_inner_cut"
  BaseFeature = -> Pocket
  Direction = (0,0,-1)
  Length = 0.65
  Length2 = 5
  Profile = -> Sketch014
  ReferenceAxis = -> Sketch014 [N_Axis]
  Refine = true
  Suppressed = false
  Type = 0
FEATURE [Sketcher::SketchObject] Sketch022  label="Top_flow_deflector_sketch"
  ArcFitTolerance = 1e-06
  FullyConstrained = true
  MakeInternals = false
  MapMode = 5
  Placement = pos=(0,0,21.3) rot=(1,0,0;3.14159rad)
  expr: Constraints[18] = Spreadsheet.B1
  expr: Constraints[3] = -abs(<<Bottom_base_sketch>>.Constraints.Offset)
  expr: Constraints[4] = <<Bottom_base_sketch>>.Constraints.Offset
  sketch-geometry (7):
    g0: LineSegment [constr] StartX=58 StartY=-23.5 StartZ=0 EndX=75 EndY=-23.5 EndZ=0
    g1: LineSegment [constr] StartX=75 StartY=-23.5 StartZ=0 EndX=75 EndY=-46.5 EndZ=0
    g2: GeomPoint X=20 Y=-20 Z=0
    g3: ArcOfCircle CenterX=49.5507 CenterY=-47.5277 CenterZ=0 NormalX=0 NormalY=0 NormalZ=1 AngleXU=0 Radius=25.4701 StartAngle=0.0403622 EndAngle=1.23265
    g4: ArcOfCircle CenterX=49.5507 CenterY=-47.5277 CenterZ=0 NormalX=0 NormalY=0 NormalZ=1 AngleXU=0 Radius=27.0701 StartAngle=0.0403622 EndAngle=1.23265
    g5: LineSegment StartX=75 StartY=-46.5 StartZ=0 EndX=76.5987 EndY=-46.4354 EndZ=0
    g6: LineSegment StartX=58 StartY=-23.5 StartZ=0 EndX=58.5308 EndY=-21.9906 EndZ=0
  constraints (20):
    c: Horizontal(g0)
    c: Coincident(g1,g0)
    c: Vertical(g1)
    c: DistanceY(g-1,g2) = -20
    c: DistanceX(g-2,g2) = 20
    c: Distance(g2,g0) = 3.5
    c: DistanceX(g2,g0) = 38
    c: Distance(g1) = 23
    c: Distance(g0) = 17
    c: Coincident(g3,g0)
    c: Coincident(g3,g1)
    c: Coincident(g4,g3)
    c: Coincident(g5,g1)
    c: Coincident(g5,g4)
    c: Coincident(g6,g0)
    c: Coincident(g6,g4)
    c: PointOnObject(g3,g5)
    c: PointOnObject(g3,g6)
    c: Distance(g5) = 1.6
    c: Distance(g3,g0) = 35
FEATURE [Sketcher::SketchObject] Sketch023  label="Bottom_mount_holes_sketch"
  ArcFitTolerance = 1e-06
  AttachmentSupport = -> [Pocket006]
  FullyConstrained = true
  MakeInternals = false
  MapMode = 5
  Placement = pos=(0,0,4.5) rot=(0,0,1;0rad)
  expr: Constraints[2] = <<Bottom_base_sketch>>.Constraints.Offset
  expr: Constraints[3] = <<Bottom_base_sketch>>.Constraints.Offset
  expr: Constraints[7] = <<Bottom_base_sketch>>.Constraints.Short_length
  sketch-geometry (3):
    g0: Circle CenterX=33.9 CenterY=22.35 CenterZ=0 NormalX=0 NormalY=0 NormalZ=1 AngleXU=0 Radius=1.4
    g1: Circle CenterX=86 CenterY=55.35 CenterZ=0 NormalX=0 NormalY=0 NormalZ=1 AngleXU=0 Radius=1.4
    g2: GeomPoint X=20 Y=20 Z=0
  constraints (8):
    c: Equal(g0,g1)
    c: Diameter(g0) = 2.8
    c: DistanceX(g-2,g2) = 20
    c: DistanceY(g-1,g2) = 20
    c: DistanceY(g2,g0) = 2.35
    c: DistanceX(g2,g0) = 13.9
    c: DistanceY(g0,g1) = 33
    c: DistanceX(g2,g1) = 66
FEATURE [PartDesign::Pocket] Pocket014  label="Bottom_mount_holes"
  BaseFeature = -> Pocket006
  Direction = (0,0,-1)
  Length = 4
  Length2 = 5
  Profile = -> Sketch023
  ReferenceAxis = -> Sketch023 [N_Axis]
  Refine = true
  Suppressed = false
  Type = 0
  expr: Length = Spreadsheet.B2 + 2.5 mm
FEATURE [PartDesign::Chamfer] Chamfer  label="Bottom_pcb_pin_chamfers"
  Angle = 45
  Base = -> Pocket014 [Edge147,Edge146]
  BaseFeature = -> Pocket014
  ChamferType = 1
  FlipDirection = false
  Refine = true
  Size = 1
  Size2 = 2
  SupportTransform = false
  Suppressed = false
  UseAllEdges = false
FEATURE [PartDesign::Fillet] Fillet  label="Bottom_corner_fillets"
  Base = -> Chamfer [Edge167,Edge183,Edge161,Edge158]
  BaseFeature = -> Chamfer
  Radius = 3.3
  Refine = true
  SupportTransform = false
  Suppressed = false
  UseAllEdges = false
  expr: Radius = <<Bottom_outer_wall_sketch>>.Constraints.Wall_thickness
FEATURE [PartDesign::Fillet] Fillet001  label="Bottom_fan_corner_fillet"
  Base = -> Fillet [Edge136]
  BaseFeature = -> Fillet
  Radius = 1.6
  Refine = true
  SupportTransform = false
  Suppressed = false
  UseAllEdges = false
  expr: Radius = Spreadsheet.B1
FEATURE [PartDesign::Fillet] Fillet002  label="Bottom_fan_inlet_fillets"
  Base = -> Fillet001 [Edge182,Edge127,Edge99,Edge101]
  BaseFeature = -> Fillet001
  Radius = 6
  Refine = true
  SupportTransform = false
  Suppressed = false
  UseAllEdges = false
FEATURE [PartDesign::Body] Body  label="Bottom"
  AllowCompound = false
  Group = -> [Sketch,Pad,Sketch001,Pad001,Sketch002,Sketch003,Pad002,Sketch004,Pad003,Sketch005,Pad004,Sketch007,Pocket001,Sketch008,Pocket002,Sketch009,Pocket003,Sketch010,Pocket004,Pocket,Sketch014,Pocket006,Sketch023,Pocket014,Chamfer,Fillet,Fillet001,Fillet002]
  Origin = -> Origin
  Tip = -> Fillet002
FEATURE [Sketcher::SketchObject] Sketch024  label="Top_ceiling_wall_sketch"
  ArcFitTolerance = 1e-06
  AttachmentSupport = -> [Pad006]
  FullyConstrained = true
  MakeInternals = false
  MapMode = 5
  Placement = pos=(0,0,17.8) rot=(0,0,1;0rad)
  expr: .Constraints.Radius = <<Top_wall_sketch>>.Constraints.Radius + Spreadsheet.B1
  expr: .Constraints.Wall_thickness = Spreadsheet.B1 + 0.1 mm
  expr: Constraints[24] = <<Bottom_base_sketch>>.Constraints.Outer_leftmost_distance
  expr: Constraints[25] = <<Bottom_base_sketch>>.Constraints.Outer_downmost_distance
  expr: Constraints[26] = <<Bottom_base_sketch>>.Constraints.Outer_housing_width
  expr: Constraints[27] = <<Bottom_base_sketch>>.Constraints.Outer_housing_height
  expr: Constraints[28] = <<Bottom_base_sketch>>.Constraints.Fan_housing_h_length
  expr: Constraints[29] = <<Bottom_base_sketch>>.Constraints.Fan_housing_v_length
  expr: Constraints[41] = Spreadsheet.B1
  expr: Constraints[43] = <<Bottom_outer_wall_sketch>>.Constraints.Wall_thickness
  expr: Constraints[48] = <<Bottom_outer_wall_sketch>>.Constraints.Breakout_wall_thickness
  expr: Constraints[53] = .Constraints.Radius
  expr: Constraints[58] = .Constraints.Wall_thickness
  expr: Constraints[59] = Spreadsheet.B1
  expr: Constraints[60] = <<Bottom_screw_tunnels_sketch>>.Constraints.Top_hole_distance
  sketch-geometry (21):
    g0: LineSegment StartX=3.9 StartY=49.3 StartZ=0 EndX=3.9 EndY=15.8 EndZ=0
    g1: LineSegment StartX=3.9 StartY=15.8 StartZ=0 EndX=96.8 EndY=15.8 EndZ=0
    g2: LineSegment StartX=96.8 StartY=15.8 StartZ=0 EndX=96.8 EndY=77.5 EndZ=0
    g3: LineSegment StartX=96.8 StartY=77.5 StartZ=0 EndX=13.3 EndY=77.5 EndZ=0
    g4: LineSegment StartX=13.3 StartY=77.5 StartZ=0 EndX=13.3 EndY=49.3 EndZ=0
    g5: LineSegment StartX=13.3 StartY=49.3 StartZ=0 EndX=3.9 EndY=49.3 EndZ=0
    g6: LineSegment StartX=21.5 StartY=75.9 StartZ=0 EndX=88.6 EndY=75.9 EndZ=0
    g7: LineSegment StartX=88.6 StartY=75.9 StartZ=0 EndX=88.6 EndY=74.2 EndZ=0
    g8: LineSegment StartX=91.7 StartY=69.6426 StartZ=0 EndX=91.7 EndY=23.6574 EndZ=0
    g9: LineSegment StartX=88.6 StartY=17.4 StartZ=0 EndX=16.6 EndY=17.4 EndZ=0
    g10: LineSegment StartX=16.6 StartY=17.4 StartZ=0 EndX=16.6 EndY=69.3 EndZ=0
    g11: LineSegment StartX=21.5 StartY=75.9 StartZ=0 EndX=21.5 EndY=74.2 EndZ=0
    g12: ArcOfCircle CenterX=16.6 CenterY=74.2 CenterZ=0 NormalX=0 NormalY=0 NormalZ=1 AngleXU=0 Radius=4.9 StartAngle=4.71239 EndAngle=6.28319
    g13: ArcOfCircle CenterX=93.5 CenterY=74.2 CenterZ=0 NormalX=0 NormalY=0 NormalZ=1 AngleXU=0 Radius=4.9 StartAngle=3.14159 EndAngle=4.33623
    g14: LineSegment StartX=88.6 StartY=17.4 StartZ=0 EndX=88.6 EndY=19.1 EndZ=0
    g15: ArcOfCircle CenterX=93.5 CenterY=19.1 CenterZ=0 NormalX=0 NormalY=0 NormalZ=1 AngleXU=0 Radius=4.9 StartAngle=1.94695 EndAngle=3.14159
    g16: LineSegment [constr] StartX=16.6 StartY=74.2 StartZ=0 EndX=21.5 EndY=74.2 EndZ=0
    g17: LineSegment [constr] StartX=16.6 StartY=74.2 StartZ=0 EndX=16.6 EndY=69.3 EndZ=0
    g18: LineSegment [constr] StartX=88.6 StartY=74.2 StartZ=0 EndX=93.5 EndY=74.2 EndZ=0
    g19: LineSegment [constr] StartX=93.5 StartY=74.2 StartZ=0 EndX=93.5 EndY=19.1 EndZ=0
    g20: LineSegment [constr] StartX=88.6 StartY=19.1 StartZ=0 EndX=93.5 EndY=19.1 EndZ=0
  constraints (61):
    c: Vertical(g0)
    c: Coincident(g1,g0)
    c: Horizontal(g1)
    c: Coincident(g2,g1)
    c: Vertical(g2)
    c: Coincident(g3,g2)
    c: Horizontal(g3)
    c: Coincident(g4,g3)
    c: Vertical(g4)
    c: Coincident(g5,g4)
    c: Coincident(g5,g0)
    c: Horizontal(g5)
    c: Horizontal(g6)
    c: Coincident(g7,g6)
    c: Vertical(g7)
    c: Vertical(g8)
    c: Horizontal(g9)
    c: Coincident(g10,g9)
    c: Vertical(g10)
    c: Coincident(g11,g6)
    c: Vertical(g11)
    c: Coincident(g12,g11)
    c: Coincident(g12,g10)
    c: PointOnObject(g12,g10)
    c: DistanceX(g-2,g0) = 3.9
    c: DistanceY(g-1,g0) = 15.8
    c: Distance(g1) = 92.9
    c: Distance(g2) = 61.7
    c: Distance(g5) = 9.4
    c: Distance(g0) = 33.5
    c: Coincident(g13,g7)
    c: Coincident(g13,g8)
    c: Coincident(g14,g9)
    c: Vertical(g14)
    c: Coincident(g15,g14)
    c: Coincident(g15,g8)
    c: Coincident(g16,g12)
    c: Coincident(g16,g11)
    c: Coincident(g17,g12)
    c: Coincident(g17,g10)
    c: Horizontal(g16)
    c: Distance(g6,g3) = 1.6
    c: Distance(g11) = 1.7  'Wall_thickness'
    c: Distance(g10,g4) = 3.3
    c: Radius(g12) = 4.9  'Radius'
    c: Coincident(g18,g7)
    c: Coincident(g18,g13)
    c: Horizontal(g18)
    c: Distance(g8,g2) = 5.1
    c: Coincident(g19,g13)
    c: Coincident(g19,g15)
    c: Vertical(g19)
    c: PointOnObject(g11,g18)
    c: Radius(g13) = 4.9
    c: Coincident(g20,g14)
    c: Coincident(g20,g15)
    c: Horizontal(g20)
    c: PointOnObject(g14,g7)
    c: Distance(g14) = 1.7
    c: Distance(g9,g1) = 1.6
    c: DistanceX(g12,g13) = 76.9
FEATURE [PartDesign::Pad] Pad007  label="Top_ceiling_wall"
  BaseFeature = -> Pad006
  Direction = (0,0,1)
  Length = 3
  Length2 = 10
  Profile = -> Sketch024
  ReferenceAxis = -> Sketch024 [N_Axis]
  Refine = true
  Suppressed = false
  Type = 0
  expr: Length = 4.5 mm - Spreadsheet.B5
FEATURE [Sketcher::SketchObject] Sketch012  label="Top_ceiling_sketch"
  ArcFitTolerance = 1e-06
  AttachmentSupport = -> [Pad007]
  FullyConstrained = true
  MakeInternals = false
  MapMode = 5
  Placement = pos=(0,0,20.8) rot=(0,0,1;0rad)
  expr: Constraints[12] = <<Bottom_base_sketch>>.Constraints.Outer_leftmost_distance
  expr: Constraints[13] = <<Bottom_base_sketch>>.Constraints.Outer_downmost_distance
  expr: Constraints[14] = <<Bottom_base_sketch>>.Constraints.Outer_housing_width
  expr: Constraints[15] = <<Bottom_base_sketch>>.Constraints.Outer_housing_height
  expr: Constraints[16] = <<Bottom_base_sketch>>.Constraints.Fan_housing_v_length
  expr: Constraints[17] = <<Bottom_base_sketch>>.Constraints.Fan_housing_h_length
  sketch-geometry (6):
    g0: LineSegment StartX=13.3 StartY=77.5 StartZ=0 EndX=13.3 EndY=49.3 EndZ=0
    g1: LineSegment StartX=3.9 StartY=49.3 StartZ=0 EndX=13.3 EndY=49.3 EndZ=0
    g2: LineSegment StartX=3.9 StartY=15.8 StartZ=0 EndX=3.9 EndY=49.3 EndZ=0
    g3: LineSegment StartX=96.8 StartY=15.8 StartZ=0 EndX=3.9 EndY=15.8 EndZ=0
    g4: LineSegment StartX=96.8 StartY=77.5 StartZ=0 EndX=96.8 EndY=15.8 EndZ=0
    g5: LineSegment StartX=13.3 StartY=77.5 StartZ=0 EndX=96.8 EndY=77.5 EndZ=0
  constraints (18):
    c: Vertical(g0)
    c: Coincident(g1,g0)
    c: Horizontal(g1)
    c: Coincident(g2,g1)
    c: Vertical(g2)
    c: Coincident(g3,g2)
    c: Horizontal(g3)
    c: Coincident(g4,g3)
    c: Vertical(g4)
    c: Coincident(g5,g0)
    c: Coincident(g5,g4)
    c: Horizontal(g5)
    c: Distance(g-1,g2) = 3.9
    c: Distance(g-1,g3) = 15.8
    c: Distance(g3) = 92.9
    c: Distance(g4) = 61.7
    c: Distance(g2) = 33.5
    c: Distance(g1) = 9.4
FEATURE [PartDesign::Pad] Pad008  label="Top_ceiling"
  BaseFeature = -> Pad007
  Direction = (0,0,1)
  Length = 1.5
  Length2 = 10
  Profile = -> Sketch012
  ReferenceAxis = -> Sketch012 [N_Axis]
  Refine = true
  Suppressed = false
  Type = 0
  expr: Length = Spreadsheet.B5
FEATURE [Sketcher::SketchObject] Sketch013  label="Top_fan_outer_cutout_sketch"
  ArcFitTolerance = 1e-06
  AttachmentSupport = -> [Pad008]
  FullyConstrained = true
  MakeInternals = false
  MapMode = 5
  Placement = pos=(0,0,0) rot=(1,0,0;3.14159rad)
  expr: .Constraints.Nut_depth = <<Bottom_fan_outer_cut_sketch>>.Constraints.Fan_clamp_length
  expr: .Constraints.Overhang_length = Spreadsheet.B1 * 2
  expr: Constraints[28] = <<Bottom_base_sketch>>.Constraints.Fan_width
  expr: Constraints[29] = <<Bottom_base_sketch>>.Constraints.Fan_height
  expr: Constraints[31] = <<Bottom_fan_outer_cut_sketch>>.Constraints.Left_distance
  expr: Constraints[32] = -abs(<<Bottom_fan_outer_cut_sketch>>.Constraints.Bottom_distance)
  expr: Constraints[34] = .Constraints.Overhang_length
  expr: Constraints[35] = .Constraints.Nut_depth
  sketch-geometry (12):
    g0: LineSegment StartX=1.5 StartY=-22.9 StartZ=0 EndX=4.7 EndY=-22.9 EndZ=0
    g1: LineSegment StartX=4.7 StartY=-22.9 StartZ=0 EndX=4.7 EndY=-22.4 EndZ=0
    g2: LineSegment StartX=4.7 StartY=-22.4 StartZ=0 EndX=15 EndY=-22.4 EndZ=0
    g3: LineSegment StartX=15 StartY=-22.4 StartZ=0 EndX=15 EndY=-22.9 EndZ=0
    g4: LineSegment StartX=15 StartY=-22.9 StartZ=0 EndX=18.2 EndY=-22.9 EndZ=0
    g5: LineSegment StartX=18.2 StartY=-22.9 StartZ=0 EndX=18.2 EndY=-47.2 EndZ=0
    g6: LineSegment StartX=18.2 StartY=-47.2 StartZ=0 EndX=15 EndY=-47.2 EndZ=0
    g7: LineSegment StartX=15 StartY=-47.2 StartZ=0 EndX=15 EndY=-47.7 EndZ=0
    g8: LineSegment StartX=15 StartY=-47.7 StartZ=0 EndX=4.7 EndY=-47.7 EndZ=0
    g9: LineSegment StartX=4.7 StartY=-47.7 StartZ=0 EndX=4.7 EndY=-47.2 EndZ=0
    g10: LineSegment StartX=4.7 StartY=-47.2 StartZ=0 EndX=1.5 EndY=-47.2 EndZ=0
    g11: LineSegment StartX=1.5 StartY=-47.2 StartZ=0 EndX=1.5 EndY=-22.9 EndZ=0
  constraints (36):
    c: Horizontal(g0)
    c: Coincident(g1,g0)
    c: Coincident(g2,g1)
    c: Horizontal(g2)
    c: Coincident(g3,g2)
    c: Vertical(g3)
    c: Coincident(g4,g3)
    c: Horizontal(g4)
    c: Coincident(g5,g4)
    c: Vertical(g5)
    c: Coincident(g6,g5)
    c: Horizontal(g6)
    c: Coincident(g7,g6)
    c: Vertical(g7)
    c: Coincident(g8,g7)
    c: Horizontal(g8)
    c: Coincident(g9,g8)
    c: Vertical(g9)
    c: Coincident(g10,g9)
    c: Horizontal(g10)
    c: Coincident(g11,g10)
    c: Coincident(g11,g0)
    c: Vertical(g11)
    c: Vertical(g1)
    c: PointOnObject(g9,g6)
    c: PointOnObject(g0,g9)
    c: PointOnObject(g3,g0)
    c: PointOnObject(g6,g3)
    c: Distance(g8) = 10.3
    c: DistanceY(g8,g1) = 25.3
    c: Distance(g3) = 0.5  'Nut_depth'
    c: DistanceX(g-2,g1) = 4.7
    c: DistanceY(g-1,g1) = -22.4
    c: Distance(g0) = 3.2  'Overhang_length'
    c: Distance(g4) = 3.2
    c: Distance(g7) = 0.5
FEATURE [PartDesign::Pocket] Pocket015  label="Top_fan_outer_cutout"
  BaseFeature = -> Pad008
  Direction = (0,0,1)
  Length = 17.3
  Length2 = 5
  Profile = -> Sketch013
  ReferenceAxis = -> Sketch013 [N_Axis]
  Refine = true
  Suppressed = false
  Type = 0
FEATURE [Sketcher::SketchObject] Sketch015  label="Top_fan_inner_cutout_sketch"
  ArcFitTolerance = 1e-06
  AttachmentSupport = -> [Pocket015]
  FullyConstrained = true
  MakeInternals = false
  MapMode = 5
  Placement = pos=(0,0,17.3) rot=(1,0,0;3.14159rad)
  expr: .Constraints.Slot_depth = <<Top_fan_outer_cutout_sketch>>.Constraints.Nut_depth
  expr: Constraints[10] = -abs(<<Bottom_fan_outer_cut_sketch>>.Constraints.Bottom_distance)
  expr: Constraints[21] = .Constraints.Slot_depth
  expr: Constraints[22] = Spreadsheet.B1 * 1.5
  expr: Constraints[7] = <<Bottom_base_sketch>>.Constraints.Fan_width
  expr: Constraints[8] = <<Bottom_base_sketch>>.Constraints.Fan_height
  expr: Constraints[9] = <<Bottom_fan_outer_cut_sketch>>.Constraints.Left_distance
  sketch-geometry (8):
    g0: LineSegment StartX=4.7 StartY=-22.4 StartZ=0 EndX=4.7 EndY=-47.7 EndZ=0
    g1: LineSegment StartX=4.7 StartY=-47.7 StartZ=0 EndX=15 EndY=-47.7 EndZ=0
    g2: LineSegment StartX=15 StartY=-22.4 StartZ=0 EndX=4.7 EndY=-22.4 EndZ=0
    g3: LineSegment StartX=15 StartY=-22.9 StartZ=0 EndX=15 EndY=-22.4 EndZ=0
    g4: LineSegment StartX=15 StartY=-47.7 StartZ=0 EndX=15 EndY=-47.2 EndZ=0
    g5: LineSegment StartX=15 StartY=-47.2 StartZ=0 EndX=17.4 EndY=-47.2 EndZ=0
    g6: LineSegment StartX=17.4 StartY=-47.2 StartZ=0 EndX=17.4 EndY=-22.9 EndZ=0
    g7: LineSegment StartX=17.4 StartY=-22.9 StartZ=0 EndX=15 EndY=-22.9 EndZ=0
  constraints (24):
    c: Coincident(g0,g1)
    c: Coincident(g1,g4)
    c: Coincident(g3,g2)
    c: Coincident(g2,g0)
    c: Vertical(g0)
    c: Horizontal(g1)
    c: Horizontal(g2)
    c: Distance(g2) = 10.3
    c: Distance(g0) = 25.3
    c: DistanceX(g-2,g0) = 4.7
    c: DistanceY(g-1,g0) = -22.4
    c: Vertical(g3)
    c: Vertical(g4)
    c: Coincident(g5,g4)
    c: Horizontal(g5)
    c: Coincident(g6,g5)
    c: Vertical(g6)
    c: Coincident(g7,g6)
    c: Coincident(g7,g3)
    c: Horizontal(g7)
    c: Distance(g3) = 0.5  'Slot_depth'
    c: Distance(g4) = 0.5
    c: Distance(g5) = 2.4
    c: PointOnObject(g4,g3)
FEATURE [PartDesign::Pocket] Pocket016  label="Top_fan_inner_cutout"
  BaseFeature = -> Pocket015
  Direction = (0,0,1)
  Length = 0.65
  Length2 = 5
  Profile = -> Sketch015
  ReferenceAxis = -> Sketch015 [N_Axis]
  Refine = true
  Suppressed = false
  Type = 0
FEATURE [Sketcher::SketchObject] Sketch016  label="Top_fan_cable_cutout_sketch"
  ArcFitTolerance = 1e-06
  AttachmentSupport = -> [Pocket016]
  FullyConstrained = true
  MakeInternals = false
  MapMode = 5
  Placement = pos=(0,0,17.95) rot=(1,0,0;3.14159rad)
  expr: Constraints[13] = <<Bottom_base_sketch>>.Constraints.Fan_height / 2
  expr: Constraints[15] = <<Bottom_base_sketch>>.Constraints.Fan_height / 2
  expr: Constraints[16] = <<Bottom_base_sketch>>.Constraints.Fan_width
  expr: Constraints[17] = <<Top_fan_outer_cutout_sketch>>.Constraints.Nut_depth
  expr: Constraints[19] = Spreadsheet.B1 * 1.5
  expr: Constraints[8] = -abs(<<Bottom_fan_outer_cut_sketch>>.Constraints.Bottom_distance)
  expr: Constraints[9] = <<Bottom_fan_outer_cut_sketch>>.Constraints.Left_distance
  sketch-geometry (7):
    g0: LineSegment StartX=4.7 StartY=-47.7 StartZ=0 EndX=15 EndY=-47.7 EndZ=0
    g1: LineSegment StartX=4.7 StartY=-35.05 StartZ=0 EndX=17.4 EndY=-35.05 EndZ=0
    g2: LineSegment StartX=17.4 StartY=-35.05 StartZ=0 EndX=17.4 EndY=-47.2 EndZ=0
    g3: LineSegment StartX=17.4 StartY=-47.2 StartZ=0 EndX=15 EndY=-47.2 EndZ=0
    g4: LineSegment StartX=15 StartY=-47.2 StartZ=0 EndX=15 EndY=-47.7 EndZ=0
    g5: GeomPoint X=4.7 Y=-22.4 Z=0
    g6: LineSegment StartX=4.7 StartY=-35.05 StartZ=0 EndX=4.7 EndY=-47.7 EndZ=0
  constraints (20):
    c: Horizontal(g0)
    c: Horizontal(g1)
    c: Coincident(g2,g1)
    c: Vertical(g2)
    c: Coincident(g3,g2)
    c: Horizontal(g3)
    c: Coincident(g4,g3)
    c: Coincident(g4,g0)
    c: DistanceY(g-1,g5) = -22.4
    c: DistanceX(g-2,g5) = 4.7
    c: Coincident(g6,g1)
    c: Coincident(g6,g0)
    c: Vertical(g6)
    c: Distance(g6) = 12.65
    c: Vertical(g4)
    c: Distance(g5,g1) = 12.65
    c: Distance(g0) = 10.3
    c: Distance(g4) = 0.5
    c: PointOnObject(g5,g6)
    c: Distance(g3) = 2.4
FEATURE [PartDesign::Pocket] Pocket017  label="Top_fan_cable_cutout"
  BaseFeature = -> Pocket016
  Direction = (0,0,1)
  Length = 2
  Length2 = 5
  Profile = -> Sketch016
  ReferenceAxis = -> Sketch016 [N_Axis]
  Refine = true
  Suppressed = false
  Type = 0
FEATURE [Sketcher::SketchObject] Sketch017  label="Top_breakout_slot_sketch"
  ArcFitTolerance = 1e-06
  AttachmentSupport = -> [Pocket017]
  FullyConstrained = true
  MakeInternals = false
  MapMode = 5
  Placement = pos=(0,0,0) rot=(1,0,0;3.14159rad)
  expr: Constraints[14] = <<Bottom_breakout_slot_sketch>>.Constraints.Slot_width
  expr: Constraints[15] = <<Bottom_breakout_slot_sketch>>.Constraints.Slot_height
  expr: Constraints[16] = -abs(<<Bottom_base_sketch>>.Constraints.Offset)
  expr: Constraints[17] = <<Bottom_base_sketch>>.Constraints.Offset
  expr: Constraints[18] = <<Bottom_breakout_slot_sketch>>.Constraints.Horizontal_center_distance
  expr: Constraints[19] = <<Bottom_breakout_slot_sketch>>.Constraints.Vertical_center_distance
  sketch-geometry (8):
    g0: LineSegment StartX=93.3 StartY=-23.6 StartZ=0 EndX=93.3 EndY=-69.7 EndZ=0
    g1: LineSegment StartX=93.3 StartY=-69.7 StartZ=0 EndX=95.2 EndY=-69.7 EndZ=0
    g2: LineSegment StartX=95.2 StartY=-69.7 StartZ=0 EndX=95.2 EndY=-23.6 EndZ=0
    g3: LineSegment StartX=95.2 StartY=-23.6 StartZ=0 EndX=93.3 EndY=-23.6 EndZ=0
    g4: LineSegment [constr] StartX=93.3 StartY=-69.7 StartZ=0 EndX=95.2 EndY=-23.6 EndZ=0
    g5: LineSegment [constr] StartX=93.3 StartY=-23.6 StartZ=0 EndX=95.2 EndY=-69.7 EndZ=0
    g6: GeomPoint [constr] X=94.25 Y=-46.65 Z=0
    g7: GeomPoint [constr] X=20 Y=-20 Z=0
  constraints (20):
    c: Coincident(g0,g1)
    c: Coincident(g1,g2)
    c: Coincident(g2,g3)
    c: Coincident(g3,g0)
    c: Vertical(g0)
    c: Vertical(g2)
    c: Horizontal(g1)
    c: Horizontal(g3)
    c: Coincident(g4,g0)
    c: Coincident(g4,g2)
    c: Coincident(g5,g0)
    c: Coincident(g5,g1)
    c: PointOnObject(g6,g5)
    c: PointOnObject(g6,g4)
    c: Distance(g3) = 1.9
    c: Distance(g2) = 46.1
    c: DistanceY(g-1,g7) = -20
    c: DistanceX(g-2,g7) = 20
    c: DistanceX(g7,g6) = 74.25
    c: DistanceY(g6,g7) = 26.65
FEATURE [PartDesign::Pocket] Pocket018  label="Top_breakout_slot"
  BaseFeature = -> Pocket017
  Direction = (0,0,1)
  Length = 14.35
  Length2 = 5
  Profile = -> Sketch017
  ReferenceAxis = -> Sketch017 [N_Axis]
  Refine = true
  Suppressed = false
  Type = 0
  expr: Length = <<Bottom_breakout_slot>>.Length
FEATURE [Sketcher::SketchObject] Sketch018  label="Top_breakout_cutout_sketch"
  ArcFitTolerance = 1e-06
  AttachmentSupport = -> [Pocket018]
  FullyConstrained = true
  MakeInternals = false
  MapMode = 5
  Placement = pos=(0,0,0) rot=(1,0,0;3.14159rad)
  expr: Constraints[14] = <<Bottom_outer_wall_sketch>>.Constraints.Breakout_wall_thickness + 1 mm
  expr: Constraints[15] = <<Bottom_breakout_slot_cutout_sketch>>.Constraints.Height
  expr: Constraints[18] = <<Bottom_breakout_slot_sketch>>.Constraints.Horizontal_center_distance
  expr: Constraints[19] = <<Bottom_breakout_slot_sketch>>.Constraints.Vertical_center_distance
  expr: Constraints[8] = -abs(<<Bottom_base_sketch>>.Constraints.Offset)
  expr: Constraints[9] = <<Bottom_base_sketch>>.Constraints.Offset
  sketch-geometry (8):
    g0: LineSegment StartX=91.2 StartY=-26.14 StartZ=0 EndX=91.2 EndY=-67.16 EndZ=0
    g1: LineSegment StartX=91.2 StartY=-67.16 StartZ=0 EndX=97.3 EndY=-67.16 EndZ=0
    g2: LineSegment StartX=97.3 StartY=-67.16 StartZ=0 EndX=97.3 EndY=-26.14 EndZ=0
    g3: LineSegment StartX=97.3 StartY=-26.14 StartZ=0 EndX=91.2 EndY=-26.14 EndZ=0
    g4: GeomPoint X=20 Y=-20 Z=0
    g5: LineSegment [constr] StartX=91.2 StartY=-67.16 StartZ=0 EndX=97.3 EndY=-26.14 EndZ=0
    g6: LineSegment [constr] StartX=91.2 StartY=-26.14 StartZ=0 EndX=97.3 EndY=-67.16 EndZ=0
    g7: GeomPoint [constr] X=94.25 Y=-46.65 Z=0
  constraints (20):
    c: Coincident(g0,g1)
    c: Coincident(g1,g2)
    c: Coincident(g2,g3)
    c: Coincident(g3,g0)
    c: Vertical(g0)
    c: Vertical(g2)
    c: Horizontal(g1)
    c: Horizontal(g3)
    c: DistanceY(g-1,g4) = -20
    c: DistanceX(g-2,g4) = 20
    c: Coincident(g5,g0)
    c: Coincident(g5,g2)
    c: Coincident(g6,g0)
    c: Coincident(g6,g1)
    c: Distance(g3) = 6.1
    c: Distance(g2) = 41.02
    c: PointOnObject(g7,g6)
    c: PointOnObject(g7,g5)
    c: DistanceX(g4,g7) = 74.25
    c: DistanceY(g7,g4) = 26.65
FEATURE [PartDesign::Pocket] Pocket019  label="Top_breakout_cutout"
  BaseFeature = -> Pocket018
  Direction = (0,0,1)
  Length = 11.81
  Length2 = 5
  Profile = -> Sketch018
  ReferenceAxis = -> Sketch018 [N_Axis]
  Refine = true
  Suppressed = false
  Type = 0
  expr: Length = <<Bottom_breakout_slot_cutout>>.Length
FEATURE [Sketcher::SketchObject] Sketch019  label="Top_screw_tunnels_sketch"
  ArcFitTolerance = 1e-06
  AttachmentSupport = -> [Pocket019]
  FullyConstrained = true
  MakeInternals = false
  MapMode = 5
  Placement = pos=(0,0,0) rot=(1,0,0;3.14159rad)
  expr: Constraints[13] = <<Bottom_screw_tunnels_sketch>>.Constraints.Left_short_distance
  expr: Constraints[14] = <<Bottom_screw_tunnels_sketch>>.Constraints.Left_long_distance
  expr: Constraints[15] = -abs(<<Bottom_screw_tunnels_sketch>>.Constraints.Bottom_distance)
  expr: Constraints[16] = -abs(<<Bottom_screw_tunnels_sketch>>.Constraints.Vertical_distance)
  expr: Constraints[17] = <<Bottom_screw_tunnels_sketch>>.Constraints.Lower_horizontal_distance
  sketch-geometry (7):
    g0: Circle CenterX=7.2 CenterY=-19.1 CenterZ=0 NormalX=0 NormalY=0 NormalZ=1 AngleXU=0 Radius=1.6
    g1: Circle CenterX=93.5 CenterY=-19.1 CenterZ=0 NormalX=0 NormalY=0 NormalZ=1 AngleXU=0 Radius=1.6
    g2: Circle CenterX=93.5 CenterY=-74.2 CenterZ=0 NormalX=0 NormalY=0 NormalZ=1 AngleXU=0 Radius=1.6
    g3: Circle CenterX=16.6 CenterY=-74.2 CenterZ=0 NormalX=0 NormalY=0 NormalZ=1 AngleXU=0 Radius=1.6
    g4: LineSegment [constr] StartX=16.6 StartY=-74.2 StartZ=0 EndX=93.5 EndY=-74.2 EndZ=0
    g5: LineSegment [constr] StartX=93.5 StartY=-74.2 StartZ=0 EndX=93.5 EndY=-19.1 EndZ=0
    g6: LineSegment [constr] StartX=7.2 StartY=-19.1 StartZ=0 EndX=93.5 EndY=-19.1 EndZ=0
  constraints (18):
    c: Equal(g0,g1)
    c: Equal(g0,g2)
    c: Equal(g0,g3)
    c: Diameter(g0) = 3.2
    c: Coincident(g4,g3)
    c: Coincident(g4,g2)
    c: Horizontal(g4)
    c: Coincident(g5,g2)
    c: Coincident(g5,g1)
    c: Vertical(g5)
    c: Coincident(g6,g0)
    c: Coincident(g6,g1)
    c: Horizontal(g6)
    c: DistanceX(g-2,g0) = 7.2
    c: DistanceX(g-2,g3) = 16.6
    c: DistanceY(g-1,g0) = -19.1
    c: DistanceY(g-1,g2) = -74.2
    c: DistanceX(g-2,g2) = 93.5
FEATURE [PartDesign::Pocket] Pocket020  label="Top_screw_tunnels"
  BaseFeature = -> Pocket019
  Direction = (0,0,1)
  Length = 5
  Length2 = 5
  Profile = -> Sketch019
  ReferenceAxis = -> Sketch019 [N_Axis]
  Refine = true
  Suppressed = false
  Type = 1
FEATURE [Sketcher::SketchObject] Sketch020  label="Top_screw_sinks_sketch"
  ArcFitTolerance = 1e-06
  AttachmentSupport = -> [Pocket020]
  FullyConstrained = true
  MakeInternals = false
  MapMode = 5
  Placement = pos=(0,0,22.3) rot=(0,0,1;0rad)
  expr: Constraints[69] = <<Bottom_screw_tunnels_sketch>>.Constraints.Left_long_distance
  expr: Constraints[70] = <<Bottom_screw_tunnels_sketch>>.Constraints.Left_short_distance
  expr: Constraints[71] = <<Bottom_screw_tunnels_sketch>>.Constraints.Bottom_distance
  expr: Constraints[72] = <<Bottom_screw_tunnels_sketch>>.Constraints.Vertical_distance
  expr: Constraints[73] = <<Bottom_screw_tunnels_sketch>>.Constraints.Lower_horizontal_distance
  expr: Constraints[75] = .Constraints.Wall_length
  expr: Constraints[76] = .Constraints.Wall_length
  expr: Constraints[77] = .Constraints.Wall_length
  expr: Constraints[78] = .Constraints.Wall_length
  expr: Constraints[79] = <<Bottom_outer_wall_sketch>>.Constraints.Wall_thickness
  sketch-geometry (28):
    g0: LineSegment [constr] StartX=16.6 StartY=74.2 StartZ=0 EndX=93.5 EndY=74.2 EndZ=0
    g1: LineSegment [constr] StartX=93.5 StartY=74.2 StartZ=0 EndX=93.5 EndY=19.1 EndZ=0
    g2: LineSegment [constr] StartX=93.5 StartY=19.1 StartZ=0 EndX=7.2 EndY=19.1 EndZ=0
    g3: ArcOfCircle CenterX=16.6 CenterY=74.2 CenterZ=0 NormalX=0 NormalY=0 NormalZ=1 AngleXU=0 Radius=3.3 StartAngle=4.71239 EndAngle=6.28319
    g4: LineSegment [constr] StartX=16.6 StartY=74.2 StartZ=0 EndX=16.6 EndY=70.9 EndZ=0
    g5: LineSegment StartX=16.6 StartY=70.9 StartZ=0 EndX=11.6 EndY=70.9 EndZ=0
    g6: LineSegment StartX=11.6 StartY=70.9 StartZ=0 EndX=11.6 EndY=79.2 EndZ=0
    g7: LineSegment StartX=11.6 StartY=79.2 StartZ=0 EndX=19.9 EndY=79.2 EndZ=0
    g8: LineSegment StartX=19.9 StartY=79.2 StartZ=0 EndX=19.9 EndY=74.2 EndZ=0
    g9: ArcOfCircle CenterX=93.5 CenterY=74.2 CenterZ=0 NormalX=0 NormalY=0 NormalZ=1 AngleXU=0 Radius=3.3 StartAngle=3.14159 EndAngle=4.71239
    g10: LineSegment StartX=90.2 StartY=74.2 StartZ=0 EndX=90.2 EndY=79.2 EndZ=0
    g11: LineSegment StartX=90.2 StartY=79.2 StartZ=0 EndX=98.5 EndY=79.2 EndZ=0
    g12: LineSegment StartX=98.5 StartY=79.2 StartZ=0 EndX=98.5 EndY=70.9 EndZ=0
    g13: LineSegment StartX=98.5 StartY=70.9 StartZ=0 EndX=93.5 EndY=70.9 EndZ=0
    g14: ArcOfCircle CenterX=93.5 CenterY=19.1 CenterZ=0 NormalX=0 NormalY=0 NormalZ=1 AngleXU=0 Radius=3.3 StartAngle=1.5708 EndAngle=3.14159
    g15: LineSegment StartX=90.2 StartY=19.1 StartZ=0 EndX=90.2 EndY=14.1 EndZ=0
    g16: LineSegment StartX=90.2 StartY=14.1 StartZ=0 EndX=98.5 EndY=14.1 EndZ=0
    g17: LineSegment StartX=98.5 StartY=14.1 StartZ=0 EndX=98.5 EndY=22.4 EndZ=0
    g18: LineSegment StartX=93.5 StartY=22.4 StartZ=0 EndX=98.5 EndY=22.4 EndZ=0
    g19: ArcOfCircle CenterX=7.2 CenterY=19.1 CenterZ=0 NormalX=0 NormalY=0 NormalZ=1 AngleXU=0 Radius=3.3 StartAngle=5e-16 EndAngle=1.5708
    g20: LineSegment [constr] StartX=7.2 StartY=22.4 StartZ=0 EndX=7.2 EndY=19.1 EndZ=0
    g21: LineSegment StartX=7.2 StartY=22.4 StartZ=0 EndX=2.2 EndY=22.4 EndZ=0
    g22: LineSegment StartX=10.5 StartY=19.1 StartZ=0 EndX=10.5 EndY=14.1 EndZ=0
    g23: LineSegment StartX=10.5 StartY=14.1 StartZ=0 EndX=2.2 EndY=14.1 EndZ=0
    g24: LineSegment StartX=2.2 StartY=14.1 StartZ=0 EndX=2.2 EndY=22.4 EndZ=0
    g25: LineSegment [constr] StartX=10.5 StartY=14.1 StartZ=0 EndX=90.2 EndY=14.1 EndZ=0
    g26: LineSegment [constr] StartX=98.5 StartY=22.4 StartZ=0 EndX=98.5 EndY=70.9 EndZ=0
    g27: LineSegment [constr] StartX=90.2 StartY=79.2 StartZ=0 EndX=19.9 EndY=79.2 EndZ=0
  constraints (80):
    c: Horizontal(g0)
    c: Vertical(g1)
    c: Horizontal(g2)
    c: Coincident(g3,g0)
    c: PointOnObject(g3,g0)
    c: Coincident(g4,g0)
    c: Coincident(g4,g3)
    c: Vertical(g4)
    c: Coincident(g5,g3)
    c: Horizontal(g5)
    c: Coincident(g6,g5)
    c: Vertical(g6)
    c: Coincident(g7,g6)
    c: Horizontal(g7)
    c: Coincident(g8,g7)
    c: Coincident(g8,g3)
    c: Vertical(g8)
    c: Coincident(g0,g1)
    c: Coincident(g9,g0)
    c: PointOnObject(g9,g0)
    c: PointOnObject(g9,g1)
    c: Coincident(g10,g9)
    c: Vertical(g10)
    c: Coincident(g11,g10)
    c: Horizontal(g11)
    c: Coincident(g12,g11)
    c: Vertical(g12)
    c: Coincident(g13,g12)
    c: Coincident(g13,g9)
    c: Horizontal(g13)
    c: Coincident(g14,g1)
    c: PointOnObject(g14,g1)
    c: PointOnObject(g14,g2)
    c: Coincident(g15,g14)
    c: Vertical(g15)
    c: Coincident(g16,g15)
    c: Horizontal(g16)
    c: Coincident(g17,g16)
    c: Vertical(g17)
    c: Coincident(g18,g14)
    c: Coincident(g18,g17)
    c: Horizontal(g18)
    c: Coincident(g1,g2)
    c: Coincident(g19,g2)
    c: PointOnObject(g19,g2)
    c: Coincident(g20,g19)
    c: Coincident(g20,g2)
    c: Vertical(g20)
    c: Coincident(g21,g19)
    c: Horizontal(g21)
    c: Coincident(g22,g19)
    c: Vertical(g22)
    c: Coincident(g23,g22)
    c: Horizontal(g23)
    c: Coincident(g24,g23)
    c: Coincident(g24,g21)
    c: Vertical(g24)
    c: Coincident(g25,g22)
    c: Coincident(g25,g15)
    c: Horizontal(g25)
    c: Coincident(g26,g17)
    c: Coincident(g26,g12)
    c: Vertical(g26)
    c: Coincident(g27,g10)
    c: Coincident(g27,g7)
    c: Horizontal(g27)
    c: Equal(g3,g9)
    c: Equal(g3,g14)
    c: Equal(g3,g19)
    c: DistanceX(g-2,g0) = 16.6
    c: DistanceX(g-2,g2) = 7.2
    c: DistanceY(g-1,g2) = 19.1
    c: DistanceY(g-1,g0) = 74.2
    c: DistanceX(g-2,g1) = 93.5
    c: Distance(g5) = 5  'Wall_length'
    c: Distance(g8) = 5
    c: Distance(g13) = 5
    c: Distance(g15) = 5
    c: Distance(g21) = 5
    c: Radius(g3) = 3.3
FEATURE [PartDesign::Pocket] Pocket021  label="Top_screw_sinks"
  BaseFeature = -> Pocket020
  Direction = (0,0,-1)
  Length = 3.5
  Length2 = 5
  Profile = -> Sketch020
  ReferenceAxis = -> Sketch020 [N_Axis]
  Refine = true
  Suppressed = false
  Type = 0
FEATURE [PartDesign::Pad] Pad009  label="Top_flow_deflector"
  BaseFeature = -> Pocket021
  Direction = (0,-1e-16,-1)
  Length = 9
  Length2 = 10
  Profile = -> Sketch022
  ReferenceAxis = -> Sketch022 [N_Axis]
  Refine = true
  Suppressed = false
  Type = 0
FEATURE [PartDesign::Fillet] Fillet003  label="Top_corner_fillets"
  Base = -> Pad009 [Edge31,Edge54,Edge27,Edge43]
  BaseFeature = -> Pad009
  Radius = 3.3
  Refine = true
  SupportTransform = false
  Suppressed = false
  UseAllEdges = false
  expr: Radius = <<Bottom_outer_wall_sketch>>.Constraints.Wall_thickness
FEATURE [PartDesign::Fillet] Fillet004  label="Top_fan_corner_fillet"
  Base = -> Fillet003 [Edge72]
  BaseFeature = -> Fillet003
  Radius = 1.6
  Refine = true
  SupportTransform = false
  Suppressed = false
  UseAllEdges = false
  expr: Radius = Spreadsheet.B1
FEATURE [PartDesign::Fillet] Fillet005  label="Top_fan_inlet_fillets"
  Base = -> Fillet004 [Edge50,Edge171]
  BaseFeature = -> Fillet004
  Radius = 6
  Refine = true
  SupportTransform = false
  Suppressed = false
  UseAllEdges = false
FEATURE [PartDesign::Fillet] Fillet006  label="Top_screw_sink_fillets"
  Base = -> Fillet005 [Edge107,Edge113,Edge9,Edge189,Edge124,Edge194,Edge122,Edge114]
  BaseFeature = -> Fillet005
  Radius = 0.8
  Refine = true
  SupportTransform = false
  Suppressed = false
  UseAllEdges = false
  expr: Radius = Spreadsheet.B1 / 2
FEATURE [PartDesign::Fillet] Fillet007  label="Top_deflector_fillets"
  Base = -> Fillet006 [Edge280,Edge283,Edge286,Edge282]
  BaseFeature = -> Fillet006
  Radius = 0.761905
  Refine = true
  SupportTransform = false
  Suppressed = false
  UseAllEdges = false
  expr: Radius = Spreadsheet.B1 / 2.1
FEATURE [Sketcher::SketchObject] Sketch025  label="Top_vents_xy_sketch"
  ArcFitTolerance = 1e-06
  AttachmentOffset = pos=(20,20,0) rot=(0,0,1;0rad)
  FullyConstrained = false
  MakeInternals = false
  MapMode = 5
  Placement = pos=(20,20,22.3) rot=(0,0,1;0rad)
  expr: .AttachmentOffset.Base.x = <<Bottom_base_sketch>>.Constraints.Offset
  expr: .AttachmentOffset.Base.y = <<Bottom_base_sketch>>.Constraints.Offset
  sketch-geometry (110):
    g0: Circle CenterX=17.2 CenterY=46.2 CenterZ=0 NormalX=0 NormalY=0 NormalZ=-1 AngleXU=0 Radius=1
    g1: ArcOfCircle CenterX=17.2 CenterY=42.2 CenterZ=0 NormalX=0 NormalY=0 NormalZ=1 AngleXU=0 Radius=1 StartAngle=0 EndAngle=3.14159
    g2: ArcOfCircle CenterX=17.2 CenterY=40.2 CenterZ=0 NormalX=0 NormalY=0 NormalZ=1 AngleXU=0 Radius=1 StartAngle=3.14159 EndAngle=6.28319
    g3: LineSegment StartX=16.2 StartY=40.2 StartZ=0 EndX=16.2 EndY=42.2 EndZ=0
    g4: LineSegment StartX=18.2 StartY=42.2 StartZ=0 EndX=18.2 EndY=40.2 EndZ=0
    g5: Circle CenterX=17.2 CenterY=36.2 CenterZ=0 NormalX=0 NormalY=0 NormalZ=-1 AngleXU=0 Radius=1
    g6: ArcOfCircle CenterX=17.2 CenterY=32.2 CenterZ=0 NormalX=0 NormalY=0 NormalZ=1 AngleXU=0 Radius=1 StartAngle=0 EndAngle=3.14159
    g7: ArcOfCircle CenterX=17.2 CenterY=30.2 CenterZ=0 NormalX=0 NormalY=0 NormalZ=1 AngleXU=0 Radius=1 StartAngle=3.14159 EndAngle=6.28319
    g8: LineSegment StartX=16.2 StartY=30.2 StartZ=0 EndX=16.2 EndY=32.2 EndZ=0
    g9: LineSegment StartX=18.2 StartY=32.2 StartZ=0 EndX=18.2 EndY=30.2 EndZ=0
    g10: ArcOfCircle CenterX=21.2 CenterY=47.2 CenterZ=0 NormalX=0 NormalY=0 NormalZ=1 AngleXU=0 Radius=1 StartAngle=0 EndAngle=3.14159
    g11: ArcOfCircle CenterX=21.2 CenterY=45.2 CenterZ=0 NormalX=0 NormalY=0 NormalZ=1 AngleXU=0 Radius=1 StartAngle=3.14159 EndAngle=6.28319
    g12: LineSegment StartX=20.2 StartY=45.2 StartZ=0 EndX=20.2 EndY=47.2 EndZ=0
    g13: LineSegment StartX=22.2 StartY=47.2 StartZ=0 EndX=22.2 EndY=45.2 EndZ=0
    g14: Circle CenterX=21.2 CenterY=41.2 CenterZ=0 NormalX=0 NormalY=0 NormalZ=-1 AngleXU=0 Radius=1
    g15: ArcOfCircle CenterX=21.2 CenterY=37.2 CenterZ=0 NormalX=0 NormalY=0 NormalZ=1 AngleXU=0 Radius=1 StartAngle=0 EndAngle=3.14159
    g16: ArcOfCircle CenterX=21.2 CenterY=35.2 CenterZ=0 NormalX=0 NormalY=0 NormalZ=1 AngleXU=0 Radius=1 StartAngle=3.14159 EndAngle=6.28319
    g17: LineSegment StartX=20.2 StartY=35.2 StartZ=0 EndX=20.2 EndY=37.2 EndZ=0
    g18: LineSegment StartX=22.2 StartY=37.2 StartZ=0 EndX=22.2 EndY=35.2 EndZ=0
    g19: Circle CenterX=21.2 CenterY=31.2 CenterZ=0 NormalX=0 NormalY=0 NormalZ=-1 AngleXU=0 Radius=1
    g20: Circle CenterX=25.2 CenterY=46.2 CenterZ=0 NormalX=0 NormalY=0 NormalZ=-1 AngleXU=0 Radius=1
    g21: ArcOfCircle CenterX=25.2 CenterY=42.2 CenterZ=0 NormalX=0 NormalY=0 NormalZ=1 AngleXU=0 Radius=1 StartAngle=0 EndAngle=3.14159
    g22: ArcOfCircle CenterX=25.2 CenterY=40.2 CenterZ=0 NormalX=0 NormalY=0 NormalZ=1 AngleXU=0 Radius=1 StartAngle=3.14159 EndAngle=6.28319
    g23: LineSegment StartX=24.2 StartY=40.2 StartZ=0 EndX=24.2 EndY=42.2 EndZ=0
    g24: LineSegment StartX=26.2 StartY=42.2 StartZ=0 EndX=26.2 EndY=40.2 EndZ=0
    g25: Circle CenterX=25.2 CenterY=36.2 CenterZ=0 NormalX=0 NormalY=0 NormalZ=-1 AngleXU=0 Radius=1
    g26: ArcOfCircle CenterX=25.2 CenterY=32.2 CenterZ=0 NormalX=0 NormalY=0 NormalZ=1 AngleXU=0 Radius=1 StartAngle=0 EndAngle=3.14159
    g27: ArcOfCircle CenterX=25.2 CenterY=30.2 CenterZ=0 NormalX=0 NormalY=0 NormalZ=1 AngleXU=0 Radius=1 StartAngle=3.14159 EndAngle=6.28319
    g28: LineSegment StartX=24.2 StartY=30.2 StartZ=0 EndX=24.2 EndY=32.2 EndZ=0
    g29: LineSegment StartX=26.2 StartY=32.2 StartZ=0 EndX=26.2 EndY=30.2 EndZ=0
    g30: ArcOfCircle CenterX=29.2 CenterY=47.2 CenterZ=0 NormalX=0 NormalY=0 NormalZ=1 AngleXU=0 Radius=1 StartAngle=0 EndAngle=3.14159
    g31: ArcOfCircle CenterX=29.2 CenterY=45.2 CenterZ=0 NormalX=0 NormalY=0 NormalZ=1 AngleXU=0 Radius=1 StartAngle=3.14159 EndAngle=6.28319
    g32: LineSegment StartX=28.2 StartY=45.2 StartZ=0 EndX=28.2 EndY=47.2 EndZ=0
    g33: LineSegment StartX=30.2 StartY=47.2 StartZ=0 EndX=30.2 EndY=45.2 EndZ=0
    g34: Circle CenterX=29.2 CenterY=41.2 CenterZ=0 NormalX=0 NormalY=0 NormalZ=-1 AngleXU=0 Radius=1
    g35: ArcOfCircle CenterX=29.2 CenterY=37.2 CenterZ=0 NormalX=0 NormalY=0 NormalZ=1 AngleXU=0 Radius=1 StartAngle=0 EndAngle=3.14159
    g36: ArcOfCircle CenterX=29.2 CenterY=35.2 CenterZ=0 NormalX=0 NormalY=0 NormalZ=1 AngleXU=0 Radius=1 StartAngle=3.14159 EndAngle=6.28319
    g37: LineSegment StartX=28.2 StartY=35.2 StartZ=0 EndX=28.2 EndY=37.2 EndZ=0
    g38: LineSegment StartX=30.2 StartY=37.2 StartZ=0 EndX=30.2 EndY=35.2 EndZ=0
    g39: Circle CenterX=29.2 CenterY=31.2 CenterZ=0 NormalX=0 NormalY=0 NormalZ=-1 AngleXU=0 Radius=1
    g40: Circle CenterX=33.2 CenterY=46.2 CenterZ=0 NormalX=0 NormalY=0 NormalZ=-1 AngleXU=0 Radius=1
    g41: ArcOfCircle CenterX=33.2 CenterY=42.2 CenterZ=0 NormalX=0 NormalY=0 NormalZ=1 AngleXU=0 Radius=1 StartAngle=0 EndAngle=3.14159
    g42: ArcOfCircle CenterX=33.2 CenterY=40.2 CenterZ=0 NormalX=0 NormalY=0 NormalZ=1 AngleXU=0 Radius=1 StartAngle=3.14159 EndAngle=6.28319
    g43: LineSegment StartX=32.2 StartY=40.2 StartZ=0 EndX=32.2 EndY=42.2 EndZ=0
    g44: LineSegment StartX=34.2 StartY=42.2 StartZ=0 EndX=34.2 EndY=40.2 EndZ=0
    g45: Circle CenterX=33.2 CenterY=36.2 CenterZ=0 NormalX=0 NormalY=0 NormalZ=-1 AngleXU=0 Radius=1
    g46: ArcOfCircle CenterX=33.2 CenterY=32.2 CenterZ=0 NormalX=0 NormalY=0 NormalZ=1 AngleXU=0 Radius=1 StartAngle=0 EndAngle=3.14159
    g47: ArcOfCircle CenterX=33.2 CenterY=30.2 CenterZ=0 NormalX=0 NormalY=0 NormalZ=1 AngleXU=0 Radius=1 StartAngle=3.14159 EndAngle=6.28319
    g48: LineSegment StartX=32.2 StartY=30.2 StartZ=0 EndX=32.2 EndY=32.2 EndZ=0
    g49: LineSegment StartX=34.2 StartY=32.2 StartZ=0 EndX=34.2 EndY=30.2 EndZ=0
    g50: Circle CenterX=41.2 CenterY=46.2 CenterZ=0 NormalX=0 NormalY=0 NormalZ=-1 AngleXU=0 Radius=1
    g51: ArcOfCircle CenterX=41.2 CenterY=42.2 CenterZ=0 NormalX=0 NormalY=0 NormalZ=1 AngleXU=0 Radius=1 StartAngle=0 EndAngle=3.14159
    g52: ArcOfCircle CenterX=41.2 CenterY=40.2 CenterZ=0 NormalX=0 NormalY=0 NormalZ=1 AngleXU=0 Radius=1 StartAngle=3.14159 EndAngle=6.28319
    g53: LineSegment StartX=40.2 StartY=40.2 StartZ=0 EndX=40.2 EndY=42.2 EndZ=0
    g54: LineSegment StartX=42.2 StartY=42.2 StartZ=0 EndX=42.2 EndY=40.2 EndZ=0
    g55: Circle CenterX=41.2 CenterY=36.2 CenterZ=0 NormalX=0 NormalY=0 NormalZ=-1 AngleXU=0 Radius=1
    g56: ArcOfCircle CenterX=41.2 CenterY=32.2 CenterZ=0 NormalX=0 NormalY=0 NormalZ=1 AngleXU=0 Radius=1 StartAngle=0 EndAngle=3.14159
    g57: ArcOfCircle CenterX=41.2 CenterY=30.2 CenterZ=0 NormalX=0 NormalY=0 NormalZ=1 AngleXU=0 Radius=1 StartAngle=3.14159 EndAngle=6.28319
    g58: LineSegment StartX=40.2 StartY=30.2 StartZ=0 EndX=40.2 EndY=32.2 EndZ=0
    g59: LineSegment StartX=42.2 StartY=32.2 StartZ=0 EndX=42.2 EndY=30.2 EndZ=0
    g60: ArcOfCircle CenterX=45.2 CenterY=47.2 CenterZ=0 NormalX=0 NormalY=0 NormalZ=1 AngleXU=0 Radius=1 StartAngle=0 EndAngle=3.14159
    g61: ArcOfCircle CenterX=45.2 CenterY=45.2 CenterZ=0 NormalX=0 NormalY=0 NormalZ=1 AngleXU=0 Radius=1 StartAngle=3.14159 EndAngle=6.28319
    g62: LineSegment StartX=44.2 StartY=45.2 StartZ=0 EndX=44.2 EndY=47.2 EndZ=0
    g63: LineSegment StartX=46.2 StartY=47.2 StartZ=0 EndX=46.2 EndY=45.2 EndZ=0
    g64: Circle CenterX=45.2 CenterY=41.2 CenterZ=0 NormalX=0 NormalY=0 NormalZ=-1 AngleXU=0 Radius=1
    g65: ArcOfCircle CenterX=45.2 CenterY=37.2 CenterZ=0 NormalX=0 NormalY=0 NormalZ=1 AngleXU=0 Radius=1 StartAngle=0 EndAngle=3.14159
    g66: ArcOfCircle CenterX=45.2 CenterY=35.2 CenterZ=0 NormalX=0 NormalY=0 NormalZ=1 AngleXU=0 Radius=1 StartAngle=3.14159 EndAngle=6.28319
    g67: LineSegment StartX=44.2 StartY=35.2 StartZ=0 EndX=44.2 EndY=37.2 EndZ=0
    g68: LineSegment StartX=46.2 StartY=37.2 StartZ=0 EndX=46.2 EndY=35.2 EndZ=0
    g69: Circle CenterX=45.2 CenterY=31.2 CenterZ=0 NormalX=0 NormalY=0 NormalZ=-1 AngleXU=0 Radius=1
    g70: Circle CenterX=49.2 CenterY=46.2 CenterZ=0 NormalX=0 NormalY=0 NormalZ=-1 AngleXU=0 Radius=1
    g71: ArcOfCircle CenterX=49.2 CenterY=42.2 CenterZ=0 NormalX=0 NormalY=0 NormalZ=1 AngleXU=0 Radius=1 StartAngle=0 EndAngle=3.14159
    g72: ArcOfCircle CenterX=49.2 CenterY=40.2 CenterZ=0 NormalX=0 NormalY=0 NormalZ=1 AngleXU=0 Radius=1 StartAngle=3.14159 EndAngle=6.28319
    g73: LineSegment StartX=48.2 StartY=40.2 StartZ=0 EndX=48.2 EndY=42.2 EndZ=0
    g74: LineSegment StartX=50.2 StartY=42.2 StartZ=0 EndX=50.2 EndY=40.2 EndZ=0
    g75: Circle CenterX=49.2 CenterY=36.2 CenterZ=0 NormalX=0 NormalY=0 NormalZ=-1 AngleXU=0 Radius=1
    g76: ArcOfCircle CenterX=49.2 CenterY=32.2 CenterZ=0 NormalX=0 NormalY=0 NormalZ=1 AngleXU=0 Radius=1 StartAngle=0 EndAngle=3.14159
    g77: ArcOfCircle CenterX=49.2 CenterY=30.2 CenterZ=0 NormalX=0 NormalY=0 NormalZ=1 AngleXU=0 Radius=1 StartAngle=3.14159 EndAngle=6.28319
    g78: LineSegment StartX=48.2 StartY=30.2 StartZ=0 EndX=48.2 EndY=32.2 EndZ=0
    g79: LineSegment StartX=50.2 StartY=32.2 StartZ=0 EndX=50.2 EndY=30.2 EndZ=0
    g80: ArcOfCircle CenterX=53.2 CenterY=47.2 CenterZ=0 NormalX=0 NormalY=0 NormalZ=1 AngleXU=0 Radius=1 StartAngle=0 EndAngle=3.14159
    g81: ArcOfCircle CenterX=53.2 CenterY=45.2 CenterZ=0 NormalX=0 NormalY=0 NormalZ=1 AngleXU=0 Radius=1 StartAngle=3.14159 EndAngle=6.28319
    g82: LineSegment StartX=52.2 StartY=45.2 StartZ=0 EndX=52.2 EndY=47.2 EndZ=0
    g83: LineSegment StartX=54.2 StartY=47.2 StartZ=0 EndX=54.2 EndY=45.2 EndZ=0
    g84: Circle CenterX=53.2 CenterY=41.2 CenterZ=0 NormalX=0 NormalY=0 NormalZ=-1 AngleXU=0 Radius=1
    g85: ArcOfCircle CenterX=53.2 CenterY=37.2 CenterZ=0 NormalX=0 NormalY=0 NormalZ=1 AngleXU=0 Radius=1 StartAngle=0 EndAngle=3.14159
    g86: ArcOfCircle CenterX=53.2 CenterY=35.2 CenterZ=0 NormalX=0 NormalY=0 NormalZ=1 AngleXU=0 Radius=1 StartAngle=3.14159 EndAngle=6.28319
    g87: LineSegment StartX=52.2 StartY=35.2 StartZ=0 EndX=52.2 EndY=37.2 EndZ=0
    g88: LineSegment StartX=54.2 StartY=37.2 StartZ=0 EndX=54.2 EndY=35.2 EndZ=0
    g89: Circle CenterX=53.2 CenterY=31.2 CenterZ=0 NormalX=0 NormalY=0 NormalZ=-1 AngleXU=0 Radius=1
    g90: ArcOfCircle CenterX=37.2 CenterY=47.2 CenterZ=0 NormalX=0 NormalY=0 NormalZ=1 AngleXU=0 Radius=1 StartAngle=0 EndAngle=3.14159
    g91: ArcOfCircle CenterX=37.2 CenterY=45.2 CenterZ=0 NormalX=0 NormalY=0 NormalZ=1 AngleXU=0 Radius=1 StartAngle=3.14159 EndAngle=6.28319
    g92: LineSegment StartX=36.2 StartY=45.2 StartZ=0 EndX=36.2 EndY=47.2 EndZ=0
    g93: LineSegment StartX=38.2 StartY=47.2 StartZ=0 EndX=38.2 EndY=45.2 EndZ=0
    g94: Circle CenterX=37.2 CenterY=41.2 CenterZ=0 NormalX=0 NormalY=0 NormalZ=-1 AngleXU=0 Radius=1
    g95: ArcOfCircle CenterX=37.2 CenterY=37.2 CenterZ=0 NormalX=0 NormalY=0 NormalZ=1 AngleXU=0 Radius=1 StartAngle=0 EndAngle=3.14159
    g96: ArcOfCircle CenterX=37.2 CenterY=35.2 CenterZ=0 NormalX=0 NormalY=0 NormalZ=1 AngleXU=0 Radius=1 StartAngle=3.14159 EndAngle=6.28319
    g97: LineSegment StartX=36.2 StartY=35.2 StartZ=0 EndX=36.2 EndY=37.2 EndZ=0
    g98: LineSegment StartX=38.2 StartY=37.2 StartZ=0 EndX=38.2 EndY=35.2 EndZ=0
    g99: Circle CenterX=37.2 CenterY=31.2 CenterZ=0 NormalX=0 NormalY=0 NormalZ=-1 AngleXU=0 Radius=1
    g100: ArcOfCircle CenterX=13.2 CenterY=47.2 CenterZ=0 NormalX=0 NormalY=0 NormalZ=1 AngleXU=0 Radius=1 StartAngle=0 EndAngle=3.14159
    g101: ArcOfCircle CenterX=13.2 CenterY=45.2 CenterZ=0 NormalX=0 NormalY=0 NormalZ=1 AngleXU=0 Radius=1 StartAngle=3.14159 EndAngle=6.28319
    g102: LineSegment StartX=12.2 StartY=45.2 StartZ=0 EndX=12.2 EndY=47.2 EndZ=0
    g103: LineSegment StartX=14.2 StartY=47.2 StartZ=0 EndX=14.2 EndY=45.2 EndZ=0
    g104: Circle CenterX=13.2 CenterY=41.2 CenterZ=0 NormalX=0 NormalY=0 NormalZ=-1 AngleXU=0 Radius=1
    g105: ArcOfCircle CenterX=13.2 CenterY=37.2 CenterZ=0 NormalX=0 NormalY=0 NormalZ=1 AngleXU=0 Radius=1 StartAngle=0 EndAngle=3.14159
    g106: ArcOfCircle CenterX=13.2 CenterY=35.2 CenterZ=0 NormalX=0 NormalY=0 NormalZ=1 AngleXU=0 Radius=1 StartAngle=3.14159 EndAngle=6.28319
    g107: LineSegment StartX=12.2 StartY=35.2 StartZ=0 EndX=12.2 EndY=37.2 EndZ=0
    g108: LineSegment StartX=14.2 StartY=37.2 StartZ=0 EndX=14.2 EndY=35.2 EndZ=0
    g109: Circle CenterX=13.2 CenterY=31.2 CenterZ=0 NormalX=0 NormalY=0 NormalZ=-1 AngleXU=0 Radius=1
FEATURE [Mesh::Feature] Board_v2
  Placement = pos=(0,0,4.5) rot=(0,0,1;0rad)
  expr: .Placement.Base.z = <<Bottom_base>>.Length + 3 mm
FEATURE [Sketcher::SketchObject] Sketch027  label="_Mount_flap_base_sketch"
  ArcFitTolerance = 1e-06
  AttachmentSupport = -> [XY_Plane006]
  FullyConstrained = true
  MakeInternals = false
  MapMode = 5
  sketch-geometry (7):
    g0: ArcOfCircle CenterX=0 CenterY=0 CenterZ=0 NormalX=0 NormalY=0 NormalZ=1 AngleXU=0 Radius=4 StartAngle=0 EndAngle=3.14159
    g1: LineSegment StartX=-4 StartY=0 StartZ=0 EndX=-4 EndY=-5 EndZ=0
    g2: LineSegment StartX=4 StartY=2.6e-15 StartZ=0 EndX=4 EndY=-5 EndZ=0
    g3: LineSegment StartX=4 StartY=-5 StartZ=0 EndX=-4 EndY=-5 EndZ=0
    g4: ArcOfCircle [constr] CenterX=-3e-16 CenterY=0 CenterZ=0 NormalX=0 NormalY=0 NormalZ=1 AngleXU=0 Radius=4 StartAngle=3.14159 EndAngle=6.28319
    g5: GeomPoint [constr] X=0 Y=-4 Z=0
    g6: Circle CenterX=-3e-16 CenterY=0 CenterZ=0 NormalX=0 NormalY=0 NormalZ=1 AngleXU=0 Radius=1.75
  constraints (19):
    c: PointOnObject(g0,g-1)
    c: Diameter(g0) = 8
    c: Coincident(g1,g0)
    c: Vertical(g1)
    c: Coincident(g2,g0)
    c: Vertical(g2)
    c: Coincident(g3,g2)
    c: Coincident(g3,g1)
    c: Horizontal(g3)
    c: Coincident(g0,g-1)
    c: PointOnObject(g5,g4)
    c: PointOnObject(g5,g-2)
    c: Coincident(g4,g0)
    c: PointOnObject(g0,g-1)
    c: Coincident(g0,g4)
    c: PointOnObject(g4,g-1)
    c: Distance(g5,g3) = 1
    c: Coincident(g6,g4)
    c: Diameter(g6) = 3.5
FEATURE [PartDesign::Pad] Pad010  label="_Mount_flap_base"
  Direction = (0,0,1)
  Length = 3
  Length2 = 10
  Profile = -> Sketch027
  ReferenceAxis = -> Sketch027 [N_Axis]
  Refine = true
  Suppressed = false
  Type = 0
FEATURE [PartDesign::Body] Body004  label="_Mount_flap"
  AllowCompound = false
  Group = -> [Sketch027,Pad010]
  Origin = -> Origin006
  Tip = -> Pad010
FEATURE [App::Part] Part001  label="Design_aids"
  Group = -> [Fan,Board_v2,Body001,Body004]
  Origin = -> Origin004
FEATURE [PartDesign::FeatureBase] Clone
  BaseFeature = -> Body004
  Suppressed = false
FEATURE [PartDesign::Body] Body005  label="Bottom_mount_tl"
  AllowCompound = false
  Group = -> [Clone]
  Origin = -> Origin007
  Placement = pos=(21.5,81.6,0) rot=(0,0,1;0rad)
  Tip = -> Clone
FEATURE [PartDesign::FeatureBase] Clone001
  BaseFeature = -> Body004
  Suppressed = false
FEATURE [PartDesign::Body] Body006  label="Bottom_mount_bl"
  AllowCompound = false
  Group = -> [Clone001]
  Origin = -> Origin008
  Placement = pos=(12.5,11.6,0) rot=(0,0,1;3.14159rad)
  Tip = -> Clone001
FEATURE [PartDesign::FeatureBase] Clone002
  BaseFeature = -> Body004
  Suppressed = false
FEATURE [PartDesign::Body] Body007  label="Bottom_mount_tr"
  AllowCompound = false
  Group = -> [Clone002]
  Origin = -> Origin009
  Placement = pos=(88.5,81.6,0) rot=(0,0,1;0rad)
  Tip = -> Clone002
FEATURE [PartDesign::FeatureBase] Clone003
  BaseFeature = -> Body004
  Suppressed = false
FEATURE [PartDesign::Body] Body008  label="Bottom_mount_br"
  AllowCompound = false
  Group = -> [Clone003]
  Origin = -> Origin010
  Placement = pos=(88.5,11.6,0) rot=(0,0,1;3.14159rad)
  Tip = -> Clone003
FEATURE [Sketcher::SketchObject] Sketch028  label="Fan_grill_base_sketch"
  ArcFitTolerance = 1e-06
  AttachmentSupport = -> [YZ_Plane011]
  FullyConstrained = true
  MakeInternals = false
  MapMode = 5
  Placement = pos=(0,0,0) rot=(0.57735,0.57735,0.57735;2.0944rad)
  sketch-geometry (18):
    g0: LineSegment StartX=-12.5 StartY=9.5 StartZ=0 EndX=-12.5 EndY=-9.5 EndZ=0
    g1: LineSegment StartX=-9.5 StartY=-12.5 StartZ=0 EndX=9.5 EndY=-12.5 EndZ=0
    g2: LineSegment StartX=12.5 StartY=-9.5 StartZ=0 EndX=12.5 EndY=9.5 EndZ=0
    g3: LineSegment StartX=9.5 StartY=12.5 StartZ=0 EndX=-9.5 EndY=12.5 EndZ=0
    g4: LineSegment [constr] StartX=-12.5 StartY=-12.5 StartZ=0 EndX=12.5 EndY=12.5 EndZ=0
    g5: LineSegment [constr] StartX=-12.5 StartY=12.5 StartZ=0 EndX=12.5 EndY=-12.5 EndZ=0
    g6: Circle CenterX=0 CenterY=0 CenterZ=0 NormalX=0 NormalY=0 NormalZ=1 AngleXU=0 Radius=2
    g7: ArcOfCircle CenterX=-9.5 CenterY=9.5 CenterZ=0 NormalX=0 NormalY=0 NormalZ=1 AngleXU=0 Radius=3 StartAngle=1.5708 EndAngle=3.14159
    g8: GeomPoint [constr] X=-12.5 Y=12.5 Z=0
    g9: ArcOfCircle CenterX=9.5 CenterY=9.5 CenterZ=0 NormalX=0 NormalY=0 NormalZ=1 AngleXU=0 Radius=3 StartAngle=0 EndAngle=1.5708
    g10: GeomPoint [constr] X=12.5 Y=12.5 Z=0
    g11: ArcOfCircle CenterX=9.5 CenterY=-9.5 CenterZ=0 NormalX=0 NormalY=0 NormalZ=1 AngleXU=0 Radius=3 StartAngle=4.71239 EndAngle=6.28319
    g12: GeomPoint [constr] X=12.5 Y=-12.5 Z=0
    g13: ArcOfCircle CenterX=-9.5 CenterY=-9.5 CenterZ=0 NormalX=0 NormalY=0 NormalZ=1 AngleXU=0 Radius=3 StartAngle=3.14159 EndAngle=4.71239
    g14: GeomPoint [constr] X=-12.5 Y=-12.5 Z=0
    g15: LineSegment [constr] StartX=-12.5 StartY=-9.5 StartZ=0 EndX=12.5 EndY=-9.5 EndZ=0
    g16: LineSegment [constr] StartX=-9.5 StartY=12.5 StartZ=0 EndX=-9.5 EndY=-12.5 EndZ=0
    g17: LineSegment [constr] StartX=-12.5 StartY=9.5 StartZ=0 EndX=12.5 EndY=9.5 EndZ=0
  constraints (40):
    c: Vertical(g0)
    c: Vertical(g2)
    c: Horizontal(g1)
    c: Horizontal(g3)
    c: Distance(g10,g8) = 25
    c: Distance(g12,g10) = 25
    c: Coincident(g4,g14)
    c: Coincident(g4,g10)
    c: Coincident(g5,g8)
    c: Coincident(g5,g12)
    c: PointOnObject(g-1,g4)
    c: PointOnObject(g-1,g5)
    c: Coincident(g6,g-1)
    c: Diameter(g6) = 4
    c: PointOnObject(g8,g3)
    c: PointOnObject(g8,g0)
    c: Tangent(g3,g7) = -1.5708
    c: Tangent(g0,g7) = -1.5708
    c: PointOnObject(g10,g3)
    c: PointOnObject(g10,g2)
    c: Tangent(g3,g9) = -1.5708
    c: Tangent(g2,g9) = -1.5708
    c: PointOnObject(g12,g2)
    c: PointOnObject(g12,g1)
    c: Tangent(g2,g11) = -1.5708
    c: Tangent(g1,g11) = -1.5708
    c: PointOnObject(g14,g0)
    c: PointOnObject(g14,g1)
    c: Tangent(g0,g13) = -1.5708
    c: Tangent(g1,g13) = -1.5708
    c: Coincident(g15,g0)
    c: Coincident(g15,g2)
    c: Horizontal(g15)
    c: Coincident(g16,g3)
    c: Coincident(g16,g1)
    c: Vertical(g16)
    c: Coincident(g17,g0)
    c: Coincident(g17,g2)
    c: Horizontal(g17)
    c: Radius(g11) = 3
FEATURE [PartDesign::Pad] Pad011  label="Fan_grill_base"
  Direction = (1,0,0)
  Length = 1.05
  Length2 = 10
  Placement = pos=(0,0,0) rot=(1,1,1;2.0944rad)
  Profile = -> Sketch028
  ReferenceAxis = -> Sketch028 [N_Axis]
  Refine = true
  Suppressed = false
  Type = 0
FEATURE [Sketcher::SketchObject] Sketch029  label="Fan_grill_inner_cutout_sketch"
  ArcFitTolerance = 1e-06
  AttachmentSupport = -> [Pad011]
  FullyConstrained = true
  MakeInternals = false
  MapMode = 5
  Placement = pos=(1.05,0,0) rot=(0.57735,0.57735,0.57735;2.0944rad)
  sketch-geometry (15):
    g0: LineSegment [constr] StartX=-12.5 StartY=12.5 StartZ=0 EndX=-12.5 EndY=-12.5 EndZ=0
    g1: LineSegment [constr] StartX=-12.5 StartY=-12.5 StartZ=0 EndX=12.5 EndY=-12.5 EndZ=0
    g2: LineSegment [constr] StartX=12.5 StartY=-12.5 StartZ=0 EndX=12.5 EndY=12.5 EndZ=0
    g3: LineSegment [constr] StartX=12.5 StartY=12.5 StartZ=0 EndX=-12.5 EndY=12.5 EndZ=0
    g4: LineSegment [constr] StartX=12.5 StartY=12.5 StartZ=0 EndX=-12.5 EndY=-12.5 EndZ=0
    g5: LineSegment [constr] StartX=-12.5 StartY=12.5 StartZ=0 EndX=12.5 EndY=-12.5 EndZ=0
    g6: Circle [constr] CenterX=0 CenterY=0 CenterZ=0 NormalX=0 NormalY=0 NormalZ=1 AngleXU=0 Radius=4
    g7: ArcOfCircle CenterX=0 CenterY=0 CenterZ=0 NormalX=0 NormalY=0 NormalZ=1 AngleXU=0 Radius=4 StartAngle=1.2232 EndAngle=1.91839
    g8: ArcOfCircle CenterX=0 CenterY=0 CenterZ=0 NormalX=0 NormalY=0 NormalZ=1 AngleXU=0 Radius=6.5 StartAngle=1.2232 EndAngle=1.91839
    g9: ArcOfCircle CenterX=-1.78836 CenterY=4.93602 CenterZ=0 NormalX=0 NormalY=0 NormalZ=1 AngleXU=0 Radius=1.25 StartAngle=1.91839 EndAngle=5.05999
    g10: ArcOfCircle CenterX=1.78836 CenterY=4.93602 CenterZ=0 NormalX=0 NormalY=0 NormalZ=1 AngleXU=0 Radius=1.25 StartAngle=4.36479 EndAngle=7.50638
    g11: LineSegment [constr] StartX=-2.21417 StartY=6.11126 StartZ=0 EndX=0 EndY=0 EndZ=0
    g12: LineSegment [constr] StartX=2.21417 StartY=6.11126 StartZ=0 EndX=0 EndY=0 EndZ=0
    g13: LineSegment [constr] StartX=-2.21417 StartY=6.11126 StartZ=0 EndX=2.21417 EndY=6.11126 EndZ=0
    g14: LineSegment [constr] StartX=0 StartY=0 StartZ=0 EndX=-2.82843 EndY=4.24264 EndZ=0
  constraints (40):
    c: Coincident(g0,g1)
    c: Coincident(g1,g2)
    c: Coincident(g2,g3)
    c: Coincident(g3,g0)
    c: Vertical(g0)
    c: Vertical(g2)
    c: Horizontal(g1)
    c: Horizontal(g3)
    c: Coincident(g4,g2)
    c: Coincident(g4,g0)
    c: Coincident(g5,g0)
    c: Coincident(g5,g1)
    c: Distance(g3) = 25
    c: Distance(g0) = 25
    c: PointOnObject(g-1,g4)
    c: PointOnObject(g-1,g5)
    c: Coincident(g6,g-1)
    c: Diameter(g6) = 8
    c: Coincident(g7,g6)
    c: Coincident(g8,g6)
    c: Coincident(g9,g8)
    c: Coincident(g9,g7)
    c: Coincident(g10,g8)
    c: Coincident(g10,g7)
    c: Coincident(g11,g8)
    c: Coincident(g11,g6)
    c: Coincident(g12,g8)
    c: Coincident(g12,g6)
    c: PointOnObject(g7,g11)
    c: PointOnObject(g9,g11)
    c: PointOnObject(g10,g12)
    c: PointOnObject(g7,g12)
    c: Diameter(g7) = 8
    c: Distance(g8,g7) = 2.5
    c: Coincident(g13,g8)
    c: Coincident(g13,g8)
    c: Horizontal(g13)
    c: Coincident(g14,g6)
    c: Tangent(g14,g9) = 1.5708
    c: Distance(g14,g5) = 1
FEATURE [PartDesign::Pocket] Pocket023  label="Fan_grill_inner_cutout"
  BaseFeature = -> Pad011
  Direction = (-1,0,0)
  Length = 5
  Length2 = 5
  Placement = pos=(0,0,0) rot=(1,1,1;2.0944rad)
  Profile = -> Sketch029
  ReferenceAxis = -> Sketch029 [N_Axis]
  Refine = true
  Suppressed = false
  Type = 1
FEATURE [PartDesign::PolarPattern] PolarPattern  label="Fan_grill_inner_cutouts"
  Angle = 360
  Axis = -> Sketch029 [N_Axis]
  BaseFeature = -> Pocket023
  Mode = 0
  Occurrences = 4
  Offset = 120
  Originals = -> [Pocket023]
  Placement = pos=(0,0,0) rot=(1,1,1;2.0944rad)
  Refine = true
  Suppressed = false
  TransformMode = 0
FEATURE [Sketcher::SketchObject] Sketch030  label="Fan_grill_outer_cutout_sketch"
  ArcFitTolerance = 1e-06
  AttachmentSupport = -> [PolarPattern]
  FullyConstrained = true
  MakeInternals = false
  MapMode = 5
  Placement = pos=(1.05,0,0) rot=(0.57735,0.57735,0.57735;2.0944rad)
  sketch-geometry (14):
    g0: LineSegment [constr] StartX=-12.5 StartY=12.5 StartZ=0 EndX=-12.5 EndY=-12.5 EndZ=0
    g1: LineSegment [constr] StartX=-12.5 StartY=-12.5 StartZ=0 EndX=12.5 EndY=-12.5 EndZ=0
    g2: LineSegment [constr] StartX=12.5 StartY=-12.5 StartZ=0 EndX=12.5 EndY=12.5 EndZ=0
    g3: LineSegment [constr] StartX=12.5 StartY=12.5 StartZ=0 EndX=-12.5 EndY=12.5 EndZ=0
    g4: LineSegment [constr] StartX=-12.5 StartY=-12.5 StartZ=0 EndX=12.5 EndY=12.5 EndZ=0
    g5: LineSegment [constr] StartX=-12.5 StartY=12.5 StartZ=0 EndX=12.5 EndY=-12.5 EndZ=0
    g6: ArcOfCircle CenterX=0 CenterY=0 CenterZ=0 NormalX=0 NormalY=0 NormalZ=1 AngleXU=0 Radius=8.5 StartAngle=1.80296 EndAngle=2.90943
    g7: ArcOfCircle CenterX=0 CenterY=0 CenterZ=0 NormalX=0 NormalY=0 NormalZ=1 AngleXU=0 Radius=11 StartAngle=1.80296 EndAngle=2.90943
    g8: ArcOfCircle CenterX=-2.2433 CenterY=9.48842 CenterZ=0 NormalX=0 NormalY=0 NormalZ=1 AngleXU=0 Radius=1.25 StartAngle=4.94455 EndAngle=8.08614
    g9: ArcOfCircle CenterX=-9.48842 CenterY=2.2433 CenterZ=0 NormalX=0 NormalY=0 NormalZ=1 AngleXU=0 Radius=1.25 StartAngle=2.90943 EndAngle=6.05102
    g10: LineSegment [constr] StartX=-2.5309 StartY=10.7049 StartZ=0 EndX=0 EndY=0 EndZ=0
    g11: LineSegment [constr] StartX=-10.7049 StartY=2.5309 StartZ=0 EndX=0 EndY=0 EndZ=0
    g12: LineSegment [constr] StartX=-10.7049 StartY=2.5309 StartZ=0 EndX=-2.5309 EndY=10.7049 EndZ=0
    g13: LineSegment [constr] StartX=0 StartY=0 StartZ=0 EndX=-1 EndY=9.61769 EndZ=0
  constraints (38):
    c: Coincident(g0,g1)
    c: Coincident(g1,g2)
    c: Coincident(g2,g3)
    c: Coincident(g3,g0)
    c: Vertical(g0)
    c: Vertical(g2)
    c: Horizontal(g1)
    c: Horizontal(g3)
    c: Distance(g3) = 25
    c: Distance(g0) = 25
    c: Coincident(g4,g0)
    c: Coincident(g4,g2)
    c: Coincident(g5,g0)
    c: Coincident(g5,g1)
    c: PointOnObject(g-1,g5)
    c: PointOnObject(g-1,g4)
    c: Coincident(g6,g-1)
    c: Coincident(g7,g6)
    c: Coincident(g8,g7)
    c: Coincident(g8,g6)
    c: Coincident(g9,g7)
    c: Coincident(g9,g6)
    c: Coincident(g10,g7)
    c: Coincident(g10,g6)
    c: Coincident(g11,g7)
    c: Coincident(g11,g6)
    c: PointOnObject(g9,g11)
    c: PointOnObject(g6,g11)
    c: PointOnObject(g8,g10)
    c: PointOnObject(g6,g10)
    c: Diameter(g6) = 17
    c: Distance(g6,g7) = 2.5
    c: Coincident(g12,g7)
    c: Coincident(g12,g7)
    c: Perpendicular(g5,g12)
    c: Coincident(g13,g6)
    c: Tangent(g13,g8) = -1.5708
    c: DistanceX(g-2,g13) = -1
FEATURE [PartDesign::Pocket] Pocket024  label="Fan_grill_outer_cutout"
  BaseFeature = -> PolarPattern
  Direction = (-1,0,0)
  Length = 5
  Length2 = 5
  Placement = pos=(0,0,0) rot=(1,1,1;2.0944rad)
  Profile = -> Sketch030
  ReferenceAxis = -> Sketch030 [N_Axis]
  Refine = true
  Suppressed = false
  Type = 1
FEATURE [PartDesign::PolarPattern] PolarPattern001  label="Fan_grill_outer_cutouts"
  Angle = 360
  Axis = -> Sketch030 [N_Axis]
  BaseFeature = -> Pocket024
  Mode = 0
  Occurrences = 4
  Offset = 120
  Originals = -> [Pocket024]
  Placement = pos=(0,0,0) rot=(1,1,1;2.0944rad)
  Refine = true
  Suppressed = false
  TransformMode = 0
FEATURE [Sketcher::SketchObject] Sketch031  label="Fan_grill_frame_sketch"
  ArcFitTolerance = 1e-06
  AttachmentSupport = -> [PolarPattern001]
  FullyConstrained = true
  MakeInternals = false
  MapMode = 5
  Placement = pos=(1.05,0,0) rot=(0.57735,0.57735,0.57735;2.0944rad)
  sketch-geometry (29):
    g0: LineSegment StartX=-12.5 StartY=9.5 StartZ=0 EndX=-12.5 EndY=-9.5 EndZ=0
    g1: LineSegment StartX=-9.5 StartY=-12.5 StartZ=0 EndX=9.5 EndY=-12.5 EndZ=0
    g2: LineSegment StartX=12.5 StartY=-9.5 StartZ=0 EndX=12.5 EndY=9.5 EndZ=0
    g3: LineSegment StartX=9.5 StartY=12.5 StartZ=0 EndX=-9.5 EndY=12.5 EndZ=0
    g4: LineSegment StartX=-11.7 StartY=9.5 StartZ=0 EndX=-11.7 EndY=-9.5 EndZ=0
    g5: LineSegment StartX=-9.5 StartY=-11.7 StartZ=0 EndX=9.5 EndY=-11.7 EndZ=0
    g6: LineSegment StartX=11.7 StartY=-9.5 StartZ=0 EndX=11.7 EndY=9.5 EndZ=0
    g7: LineSegment StartX=9.5 StartY=11.7 StartZ=0 EndX=-9.5 EndY=11.7 EndZ=0
    g8: LineSegment [constr] StartX=-12.5 StartY=-12.5 StartZ=0 EndX=12.5 EndY=12.5 EndZ=0
    g9: LineSegment [constr] StartX=-12.5 StartY=12.5 StartZ=0 EndX=12.5 EndY=-12.5 EndZ=0
    g10: ArcOfCircle CenterX=-9.5 CenterY=9.5 CenterZ=0 NormalX=0 NormalY=0 NormalZ=1 AngleXU=0 Radius=2.2 StartAngle=1.5708 EndAngle=3.14159
    g11: GeomPoint [constr] X=-11.7 Y=11.7 Z=0
    g12: ArcOfCircle CenterX=9.5 CenterY=9.5 CenterZ=0 NormalX=0 NormalY=0 NormalZ=1 AngleXU=0 Radius=2.2 StartAngle=4e-16 EndAngle=1.5708
    g13: GeomPoint [constr] X=11.7 Y=11.7 Z=0
    g14: ArcOfCircle CenterX=9.5 CenterY=-9.5 CenterZ=0 NormalX=0 NormalY=0 NormalZ=1 AngleXU=0 Radius=2.2 StartAngle=4.71239 EndAngle=6.28319
    g15: GeomPoint [constr] X=11.7 Y=-11.7 Z=0
    g16: ArcOfCircle CenterX=-9.5 CenterY=-9.5 CenterZ=0 NormalX=0 NormalY=0 NormalZ=1 AngleXU=0 Radius=2.2 StartAngle=3.14159 EndAngle=4.71239
    g17: GeomPoint [constr] X=-11.7 Y=-11.7 Z=0
    g18: LineSegment [constr] StartX=-11.7 StartY=9.5 StartZ=0 EndX=11.7 EndY=9.5 EndZ=0
    g19: LineSegment [constr] StartX=9.5 StartY=11.7 StartZ=0 EndX=9.5 EndY=-11.7 EndZ=0
    g20: LineSegment [constr] StartX=11.7 StartY=-9.5 StartZ=0 EndX=-11.7 EndY=-9.5 EndZ=0
    g21: ArcOfCircle CenterX=-9.5 CenterY=9.5 CenterZ=0 NormalX=0 NormalY=0 NormalZ=1 AngleXU=0 Radius=3 StartAngle=1.5708 EndAngle=3.14159
    g22: GeomPoint [constr] X=-12.5 Y=12.5 Z=0
    g23: ArcOfCircle CenterX=9.5 CenterY=9.5 CenterZ=0 NormalX=0 NormalY=0 NormalZ=1 AngleXU=0 Radius=3 StartAngle=0 EndAngle=1.5708
    g24: GeomPoint [constr] X=12.5 Y=12.5 Z=0
    g25: ArcOfCircle CenterX=9.5 CenterY=-9.5 CenterZ=0 NormalX=0 NormalY=0 NormalZ=1 AngleXU=0 Radius=3 StartAngle=4.71239 EndAngle=6.28319
    g26: GeomPoint [constr] X=12.5 Y=-12.5 Z=0
    g27: ArcOfCircle CenterX=-9.5 CenterY=-9.5 CenterZ=0 NormalX=0 NormalY=0 NormalZ=1 AngleXU=0 Radius=3 StartAngle=3.14159 EndAngle=4.71239
    g28: GeomPoint [constr] X=-12.5 Y=-12.5 Z=0
  constraints (66):
    c: Vertical(g0)
    c: Vertical(g2)
    c: Horizontal(g1)
    c: Horizontal(g3)
    c: Vertical(g4)
    c: Vertical(g6)
    c: Horizontal(g5)
    c: Horizontal(g7)
    c: Coincident(g8,g28)
    c: Coincident(g8,g24)
    c: Coincident(g9,g22)
    c: Coincident(g9,g26)
    c: PointOnObject(g-1,g8)
    c: PointOnObject(g-1,g9)
    c: PointOnObject(g11,g9)
    c: PointOnObject(g13,g8)
    c: PointOnObject(g15,g9)
    c: Distance(g24,g22) = 25
    c: Distance(g28,g22) = 25
    c: Distance(g11,g3) = 0.8
    c: PointOnObject(g11,g7)
    c: PointOnObject(g11,g4)
    c: Tangent(g7,g10) = -1.5708
    c: Tangent(g4,g10) = -1.5708
    c: PointOnObject(g13,g7)
    c: PointOnObject(g13,g6)
    c: Tangent(g7,g12) = -1.5708
    c: Tangent(g6,g12) = -1.5708
    c: PointOnObject(g15,g6)
    c: PointOnObject(g15,g5)
    c: Tangent(g6,g14) = -1.5708
    c: Tangent(g5,g14) = -1.5708
    c: PointOnObject(g17,g5)
    c: PointOnObject(g17,g4)
    c: Tangent(g5,g16) = -1.5708
    c: Tangent(g4,g16) = -1.5708
    c: Coincident(g18,g4)
    c: Coincident(g18,g6)
    c: Horizontal(g18)
    c: Coincident(g19,g7)
    c: Coincident(g19,g5)
    c: Vertical(g19)
    c: Coincident(g20,g6)
    c: Coincident(g20,g4)
    c: Horizontal(g20)
    c: PointOnObject(g22,g3)
    c: PointOnObject(g22,g0)
    c: Tangent(g3,g21) = -1.5708
    c: Tangent(g0,g21) = -1.5708
    c: PointOnObject(g24,g3)
    c: PointOnObject(g24,g2)
    c: Tangent(g3,g23) = -1.5708
    c: Tangent(g2,g23) = -1.5708
    c: PointOnObject(g26,g2)
    c: PointOnObject(g26,g1)
    c: Tangent(g2,g25) = -1.5708
    c: Tangent(g1,g25) = -1.5708
    c: PointOnObject(g28,g1)
    c: PointOnObject(g28,g0)
    c: Tangent(g1,g27) = -1.5708
    c: Tangent(g0,g27) = -1.5708
    c: PointOnObject(g0,g20)
    c: PointOnObject(g1,g19)
    c: PointOnObject(g3,g19)
    c: PointOnObject(g0,g18)
    c: Radius(g25) = 3
FEATURE [PartDesign::Pad] Pad012  label="Fan_grill_frame"
  BaseFeature = -> PolarPattern001
  Direction = (1,0,0)
  Length = 0.75
  Length2 = 10
  Placement = pos=(0,0,0) rot=(1,1,1;2.0944rad)
  Profile = -> Sketch031
  ReferenceAxis = -> Sketch031 [N_Axis]
  Refine = true
  Suppressed = false
  Type = 0
FEATURE [PartDesign::Body] Body009  label="Fan_grill"
  AllowCompound = false
  Group = -> [Sketch028,Pad011,Sketch029,Pocket023,PolarPattern,Sketch030,Pocket024,PolarPattern001,Sketch031,Pad012]
  Origin = -> Origin011
  Placement = pos=(4.85,35.05,22.7) rot=(0,0,1;0rad)
  Tip = -> Pad012
  expr: .Placement.Base.z = <<Bottom_base>>.Length + <<Bottom_outer_wall>>.Length - <<Bottom_fan_outer_cut>>.Length - <<Bottom_fan_inner_cut>>.Length + 12.65 mm
FEATURE [App::Part] Part002  label="Utils"
  Group = -> [Body005,Body007,Body006,Body008,Sketch025]
  Origin = -> Origin012
FEATURE [Sketcher::SketchObject] Sketch032  label="Top_vents_xyz_sketch"
  ArcFitTolerance = 1e-06
  AttachmentOffset = pos=(20,20,0) rot=(0,0,1;3.14159rad)
  AttachmentSupport = -> [Fillet007]
  FullyConstrained = false
  MakeInternals = false
  MapMode = 5
  Placement = pos=(20,20,22.3) rot=(0,0,1;3.14159rad)
  expr: .AttachmentOffset.Base.x = <<Bottom_base_sketch>>.Constraints.Offset
  expr: .AttachmentOffset.Base.y = <<Bottom_base_sketch>>.Constraints.Offset
  sketch-geometry (120):
    g0: Circle CenterX=-16.6 CenterY=-22.2 CenterZ=0 NormalX=0 NormalY=0 NormalZ=-1 AngleXU=-3.14159 Radius=1
    g1: ArcOfCircle CenterX=-16.6 CenterY=-18.2 CenterZ=0 NormalX=0 NormalY=0 NormalZ=1 AngleXU=3.14159 Radius=1 StartAngle=0 EndAngle=3.14159
    g2: ArcOfCircle CenterX=-16.6 CenterY=-16.2 CenterZ=0 NormalX=0 NormalY=0 NormalZ=1 AngleXU=3.14159 Radius=1 StartAngle=3.14159 EndAngle=6.28319
    g3: LineSegment StartX=-15.6 StartY=-16.2 StartZ=0 EndX=-15.6 EndY=-18.2 EndZ=0
    g4: LineSegment StartX=-17.6 StartY=-18.2 StartZ=0 EndX=-17.6 EndY=-16.2 EndZ=0
    g5: Circle CenterX=-16.6 CenterY=-12.2 CenterZ=0 NormalX=0 NormalY=0 NormalZ=-1 AngleXU=-3.14159 Radius=1
    g6: ArcOfCircle CenterX=-16.6 CenterY=-8.2 CenterZ=0 NormalX=0 NormalY=0 NormalZ=1 AngleXU=3.14159 Radius=1 StartAngle=0 EndAngle=3.14159
    g7: ArcOfCircle CenterX=-16.6 CenterY=-6.2 CenterZ=0 NormalX=0 NormalY=0 NormalZ=1 AngleXU=3.14159 Radius=1 StartAngle=3.14159 EndAngle=6.28319
    g8: LineSegment StartX=-15.6 StartY=-6.2 StartZ=0 EndX=-15.6 EndY=-8.2 EndZ=0
    g9: LineSegment StartX=-17.6 StartY=-8.2 StartZ=0 EndX=-17.6 EndY=-6.2 EndZ=0
    g10: ArcOfCircle CenterX=-20.6 CenterY=-23.2 CenterZ=0 NormalX=0 NormalY=0 NormalZ=1 AngleXU=3.14159 Radius=1 StartAngle=0 EndAngle=3.14159
    g11: ArcOfCircle CenterX=-20.6 CenterY=-21.2 CenterZ=0 NormalX=0 NormalY=0 NormalZ=1 AngleXU=3.14159 Radius=1 StartAngle=3.14159 EndAngle=6.28319
    g12: LineSegment StartX=-19.6 StartY=-21.2 StartZ=0 EndX=-19.6 EndY=-23.2 EndZ=0
    g13: LineSegment StartX=-21.6 StartY=-23.2 StartZ=0 EndX=-21.6 EndY=-21.2 EndZ=0
    g14: Circle CenterX=-20.6 CenterY=-17.2 CenterZ=0 NormalX=0 NormalY=0 NormalZ=-1 AngleXU=-3.14159 Radius=1
    g15: ArcOfCircle CenterX=-20.6 CenterY=-13.2 CenterZ=0 NormalX=0 NormalY=0 NormalZ=1 AngleXU=3.14159 Radius=1 StartAngle=0 EndAngle=3.14159
    g16: ArcOfCircle CenterX=-20.6 CenterY=-11.2 CenterZ=0 NormalX=0 NormalY=0 NormalZ=1 AngleXU=3.14159 Radius=1 StartAngle=3.14159 EndAngle=6.28319
    g17: LineSegment StartX=-19.6 StartY=-11.2 StartZ=0 EndX=-19.6 EndY=-13.2 EndZ=0
    g18: LineSegment StartX=-21.6 StartY=-13.2 StartZ=0 EndX=-21.6 EndY=-11.2 EndZ=0
    g19: Circle CenterX=-20.6 CenterY=-7.2 CenterZ=0 NormalX=0 NormalY=0 NormalZ=-1 AngleXU=-3.14159 Radius=1
    g20: Circle CenterX=-24.6 CenterY=-22.2 CenterZ=0 NormalX=0 NormalY=0 NormalZ=-1 AngleXU=-3.14159 Radius=1
    g21: ArcOfCircle CenterX=-24.6 CenterY=-18.2 CenterZ=0 NormalX=0 NormalY=0 NormalZ=1 AngleXU=3.14159 Radius=1 StartAngle=0 EndAngle=3.14159
    g22: ArcOfCircle CenterX=-24.6 CenterY=-16.2 CenterZ=0 NormalX=0 NormalY=0 NormalZ=1 AngleXU=3.14159 Radius=1 StartAngle=3.14159 EndAngle=6.28319
    g23: LineSegment StartX=-23.6 StartY=-16.2 StartZ=0 EndX=-23.6 EndY=-18.2 EndZ=0
    g24: LineSegment StartX=-25.6 StartY=-18.2 StartZ=0 EndX=-25.6 EndY=-16.2 EndZ=0
    g25: Circle CenterX=-24.6 CenterY=-12.2 CenterZ=0 NormalX=0 NormalY=0 NormalZ=-1 AngleXU=-3.14159 Radius=1
    g26: ArcOfCircle CenterX=-24.6 CenterY=-8.2 CenterZ=0 NormalX=0 NormalY=0 NormalZ=1 AngleXU=3.14159 Radius=1 StartAngle=0 EndAngle=3.14159
    g27: ArcOfCircle CenterX=-24.6 CenterY=-6.2 CenterZ=0 NormalX=0 NormalY=0 NormalZ=1 AngleXU=3.14159 Radius=1 StartAngle=3.14159 EndAngle=6.28319
    g28: LineSegment StartX=-23.6 StartY=-6.2 StartZ=0 EndX=-23.6 EndY=-8.2 EndZ=0
    g29: LineSegment StartX=-25.6 StartY=-8.2 StartZ=0 EndX=-25.6 EndY=-6.2 EndZ=0
    g30: ArcOfCircle CenterX=-28.6 CenterY=-23.2 CenterZ=0 NormalX=0 NormalY=0 NormalZ=1 AngleXU=3.14159 Radius=1 StartAngle=0 EndAngle=3.14159
    g31: ArcOfCircle CenterX=-28.6 CenterY=-21.2 CenterZ=0 NormalX=0 NormalY=0 NormalZ=1 AngleXU=3.14159 Radius=1 StartAngle=3.14159 EndAngle=6.28319
    g32: LineSegment StartX=-27.6 StartY=-21.2 StartZ=0 EndX=-27.6 EndY=-23.2 EndZ=0
    g33: LineSegment StartX=-29.6 StartY=-23.2 StartZ=0 EndX=-29.6 EndY=-21.2 EndZ=0
    g34: Circle CenterX=-28.6 CenterY=-17.2 CenterZ=0 NormalX=0 NormalY=0 NormalZ=-1 AngleXU=-3.14159 Radius=1
    g35: ArcOfCircle CenterX=-28.6 CenterY=-13.2 CenterZ=0 NormalX=0 NormalY=0 NormalZ=1 AngleXU=3.14159 Radius=1 StartAngle=0 EndAngle=3.14159
    g36: ArcOfCircle CenterX=-28.6 CenterY=-11.2 CenterZ=0 NormalX=0 NormalY=0 NormalZ=1 AngleXU=3.14159 Radius=1 StartAngle=3.14159 EndAngle=6.28319
    g37: LineSegment StartX=-27.6 StartY=-11.2 StartZ=0 EndX=-27.6 EndY=-13.2 EndZ=0
    g38: LineSegment StartX=-29.6 StartY=-13.2 StartZ=0 EndX=-29.6 EndY=-11.2 EndZ=0
    g39: Circle CenterX=-28.6 CenterY=-7.2 CenterZ=0 NormalX=0 NormalY=0 NormalZ=-1 AngleXU=-3.14159 Radius=1
    g40: Circle CenterX=-16.6 CenterY=-46.2 CenterZ=0 NormalX=0 NormalY=0 NormalZ=-1 AngleXU=-3.14159 Radius=1
    g41: ArcOfCircle CenterX=-16.6 CenterY=-42.2 CenterZ=0 NormalX=0 NormalY=0 NormalZ=1 AngleXU=3.14159 Radius=1 StartAngle=0 EndAngle=3.14159
    g42: ArcOfCircle CenterX=-16.6 CenterY=-40.2 CenterZ=0 NormalX=0 NormalY=0 NormalZ=1 AngleXU=3.14159 Radius=1 StartAngle=3.14159 EndAngle=6.28319
    g43: LineSegment StartX=-15.6 StartY=-40.2 StartZ=0 EndX=-15.6 EndY=-42.2 EndZ=0
    g44: LineSegment StartX=-17.6 StartY=-42.2 StartZ=0 EndX=-17.6 EndY=-40.2 EndZ=0
    g45: Circle CenterX=-16.6 CenterY=-36.2 CenterZ=0 NormalX=0 NormalY=0 NormalZ=-1 AngleXU=-3.14159 Radius=1
    g46: ArcOfCircle CenterX=-16.6 CenterY=-32.2 CenterZ=0 NormalX=0 NormalY=0 NormalZ=1 AngleXU=3.14159 Radius=1 StartAngle=0 EndAngle=3.14159
    g47: ArcOfCircle CenterX=-16.6 CenterY=-30.2 CenterZ=0 NormalX=0 NormalY=0 NormalZ=1 AngleXU=3.14159 Radius=1 StartAngle=3.14159 EndAngle=6.28319
    g48: LineSegment StartX=-15.6 StartY=-30.2 StartZ=0 EndX=-15.6 EndY=-32.2 EndZ=0
    g49: LineSegment StartX=-17.6 StartY=-32.2 StartZ=0 EndX=-17.6 EndY=-30.2 EndZ=0
    g50: ArcOfCircle CenterX=-20.6 CenterY=-47.2 CenterZ=0 NormalX=0 NormalY=0 NormalZ=1 AngleXU=3.14159 Radius=1 StartAngle=0 EndAngle=3.14159
    g51: ArcOfCircle CenterX=-20.6 CenterY=-45.2 CenterZ=0 NormalX=0 NormalY=0 NormalZ=1 AngleXU=3.14159 Radius=1 StartAngle=3.14159 EndAngle=6.28319
    g52: LineSegment StartX=-19.6 StartY=-45.2 StartZ=0 EndX=-19.6 EndY=-47.2 EndZ=0
    g53: LineSegment StartX=-21.6 StartY=-47.2 StartZ=0 EndX=-21.6 EndY=-45.2 EndZ=0
    g54: Circle CenterX=-20.6 CenterY=-41.2 CenterZ=0 NormalX=0 NormalY=0 NormalZ=-1 AngleXU=-3.14159 Radius=1
    g55: ArcOfCircle CenterX=-20.6 CenterY=-37.2 CenterZ=0 NormalX=0 NormalY=0 NormalZ=1 AngleXU=3.14159 Radius=1 StartAngle=0 EndAngle=3.14159
    g56: ArcOfCircle CenterX=-20.6 CenterY=-35.2 CenterZ=0 NormalX=0 NormalY=0 NormalZ=1 AngleXU=3.14159 Radius=1 StartAngle=3.14159 EndAngle=6.28319
    g57: LineSegment StartX=-19.6 StartY=-35.2 StartZ=0 EndX=-19.6 EndY=-37.2 EndZ=0
    g58: LineSegment StartX=-21.6 StartY=-37.2 StartZ=0 EndX=-21.6 EndY=-35.2 EndZ=0
    g59: Circle CenterX=-20.6 CenterY=-31.2 CenterZ=0 NormalX=0 NormalY=0 NormalZ=-1 AngleXU=-3.14159 Radius=1
    g60: Circle CenterX=-24.6 CenterY=-46.2 CenterZ=0 NormalX=0 NormalY=0 NormalZ=-1 AngleXU=-3.14159 Radius=1
    g61: ArcOfCircle CenterX=-24.6 CenterY=-42.2 CenterZ=0 NormalX=0 NormalY=0 NormalZ=1 AngleXU=3.14159 Radius=1 StartAngle=0 EndAngle=3.14159
    g62: ArcOfCircle CenterX=-24.6 CenterY=-40.2 CenterZ=0 NormalX=0 NormalY=0 NormalZ=1 AngleXU=3.14159 Radius=1 StartAngle=3.14159 EndAngle=6.28319
    g63: LineSegment StartX=-23.6 StartY=-40.2 StartZ=0 EndX=-23.6 EndY=-42.2 EndZ=0
    g64: LineSegment StartX=-25.6 StartY=-42.2 StartZ=0 EndX=-25.6 EndY=-40.2 EndZ=0
    g65: Circle CenterX=-24.6 CenterY=-36.2 CenterZ=0 NormalX=0 NormalY=0 NormalZ=-1 AngleXU=-3.14159 Radius=1
    g66: ArcOfCircle CenterX=-24.6 CenterY=-32.2 CenterZ=0 NormalX=0 NormalY=0 NormalZ=1 AngleXU=3.14159 Radius=1 StartAngle=0 EndAngle=3.14159
    g67: ArcOfCircle CenterX=-24.6 CenterY=-30.2 CenterZ=0 NormalX=0 NormalY=0 NormalZ=1 AngleXU=3.14159 Radius=1 StartAngle=3.14159 EndAngle=6.28319
    g68: LineSegment StartX=-23.6 StartY=-30.2 StartZ=0 EndX=-23.6 EndY=-32.2 EndZ=0
    g69: LineSegment StartX=-25.6 StartY=-32.2 StartZ=0 EndX=-25.6 EndY=-30.2 EndZ=0
    g70: ArcOfCircle CenterX=-28.6 CenterY=-47.2 CenterZ=0 NormalX=0 NormalY=0 NormalZ=1 AngleXU=3.14159 Radius=1 StartAngle=0 EndAngle=3.14159
    g71: ArcOfCircle CenterX=-28.6 CenterY=-45.2 CenterZ=0 NormalX=0 NormalY=0 NormalZ=1 AngleXU=3.14159 Radius=1 StartAngle=3.14159 EndAngle=6.28319
    g72: LineSegment StartX=-27.6 StartY=-45.2 StartZ=0 EndX=-27.6 EndY=-47.2 EndZ=0
    g73: LineSegment StartX=-29.6 StartY=-47.2 StartZ=0 EndX=-29.6 EndY=-45.2 EndZ=0
    g74: Circle CenterX=-28.6 CenterY=-41.2 CenterZ=0 NormalX=0 NormalY=0 NormalZ=-1 AngleXU=-3.14159 Radius=1
    g75: ArcOfCircle CenterX=-28.6 CenterY=-37.2 CenterZ=0 NormalX=0 NormalY=0 NormalZ=1 AngleXU=3.14159 Radius=1 StartAngle=0 EndAngle=3.14159
    g76: ArcOfCircle CenterX=-28.6 CenterY=-35.2 CenterZ=0 NormalX=0 NormalY=0 NormalZ=1 AngleXU=3.14159 Radius=1 StartAngle=3.14159 EndAngle=6.28319
    g77: LineSegment StartX=-27.6 StartY=-35.2 StartZ=0 EndX=-27.6 EndY=-37.2 EndZ=0
    g78: LineSegment StartX=-29.6 StartY=-37.2 StartZ=0 EndX=-29.6 EndY=-35.2 EndZ=0
    g79: Circle CenterX=-28.6 CenterY=-31.2 CenterZ=0 NormalX=0 NormalY=0 NormalZ=-1 AngleXU=-3.14159 Radius=1
    g80: Circle CenterX=-37.8 CenterY=-46.2 CenterZ=0 NormalX=0 NormalY=0 NormalZ=-1 AngleXU=-3.14159 Radius=1
    g81: ArcOfCircle CenterX=-37.8 CenterY=-42.2 CenterZ=0 NormalX=0 NormalY=0 NormalZ=1 AngleXU=3.14159 Radius=1 StartAngle=0 EndAngle=3.14159
    g82: ArcOfCircle CenterX=-37.8 CenterY=-40.2 CenterZ=0 NormalX=0 NormalY=0 NormalZ=1 AngleXU=3.14159 Radius=1 StartAngle=3.14159 EndAngle=6.28319
    g83: LineSegment StartX=-36.8 StartY=-40.2 StartZ=0 EndX=-36.8 EndY=-42.2 EndZ=0
    g84: LineSegment StartX=-38.8 StartY=-42.2 StartZ=0 EndX=-38.8 EndY=-40.2 EndZ=0
    g85: Circle CenterX=-37.8 CenterY=-36.2 CenterZ=0 NormalX=0 NormalY=0 NormalZ=-1 AngleXU=-3.14159 Radius=1
    g86: ArcOfCircle CenterX=-37.8 CenterY=-32.2 CenterZ=0 NormalX=0 NormalY=0 NormalZ=1 AngleXU=3.14159 Radius=1 StartAngle=0 EndAngle=3.14159
    g87: ArcOfCircle CenterX=-37.8 CenterY=-30.2 CenterZ=0 NormalX=0 NormalY=0 NormalZ=1 AngleXU=3.14159 Radius=1 StartAngle=3.14159 EndAngle=6.28319
    g88: LineSegment StartX=-36.8 StartY=-30.2 StartZ=0 EndX=-36.8 EndY=-32.2 EndZ=0
    g89: LineSegment StartX=-38.8 StartY=-32.2 StartZ=0 EndX=-38.8 EndY=-30.2 EndZ=0
    g90: ArcOfCircle CenterX=-41.8 CenterY=-47.2 CenterZ=0 NormalX=0 NormalY=0 NormalZ=1 AngleXU=3.14159 Radius=1 StartAngle=0 EndAngle=3.14159
    g91: ArcOfCircle CenterX=-41.8 CenterY=-45.2 CenterZ=0 NormalX=0 NormalY=0 NormalZ=1 AngleXU=3.14159 Radius=1 StartAngle=3.14159 EndAngle=6.28319
    g92: LineSegment StartX=-40.8 StartY=-45.2 StartZ=0 EndX=-40.8 EndY=-47.2 EndZ=0
    g93: LineSegment StartX=-42.8 StartY=-47.2 StartZ=0 EndX=-42.8 EndY=-45.2 EndZ=0
    g94: Circle CenterX=-41.8 CenterY=-41.2 CenterZ=0 NormalX=0 NormalY=0 NormalZ=-1 AngleXU=-3.14159 Radius=1
    g95: ArcOfCircle CenterX=-41.8 CenterY=-37.2 CenterZ=0 NormalX=0 NormalY=0 NormalZ=1 AngleXU=3.14159 Radius=1 StartAngle=0 EndAngle=3.14159
    g96: ArcOfCircle CenterX=-41.8 CenterY=-35.2 CenterZ=0 NormalX=0 NormalY=0 NormalZ=1 AngleXU=3.14159 Radius=1 StartAngle=3.14159 EndAngle=6.28319
    g97: LineSegment StartX=-40.8 StartY=-35.2 StartZ=0 EndX=-40.8 EndY=-37.2 EndZ=0
    g98: LineSegment StartX=-42.8 StartY=-37.2 StartZ=0 EndX=-42.8 EndY=-35.2 EndZ=0
    g99: Circle CenterX=-41.8 CenterY=-31.2 CenterZ=0 NormalX=0 NormalY=0 NormalZ=-1 AngleXU=-3.14159 Radius=1
    g100: Circle CenterX=-45.8 CenterY=-46.2 CenterZ=0 NormalX=0 NormalY=0 NormalZ=-1 AngleXU=-3.14159 Radius=1
    g101: ArcOfCircle CenterX=-45.8 CenterY=-42.2 CenterZ=0 NormalX=0 NormalY=0 NormalZ=1 AngleXU=3.14159 Radius=1 StartAngle=0 EndAngle=3.14159
    g102: ArcOfCircle CenterX=-45.8 CenterY=-40.2 CenterZ=0 NormalX=0 NormalY=0 NormalZ=1 AngleXU=3.14159 Radius=1 StartAngle=3.14159 EndAngle=6.28319
    g103: LineSegment StartX=-44.8 StartY=-40.2 StartZ=0 EndX=-44.8 EndY=-42.2 EndZ=0
    g104: LineSegment StartX=-46.8 StartY=-42.2 StartZ=0 EndX=-46.8 EndY=-40.2 EndZ=0
    g105: Circle CenterX=-45.8 CenterY=-36.2 CenterZ=0 NormalX=0 NormalY=0 NormalZ=-1 AngleXU=-3.14159 Radius=1
    g106: ArcOfCircle CenterX=-45.8 CenterY=-32.2 CenterZ=0 NormalX=0 NormalY=0 NormalZ=1 AngleXU=3.14159 Radius=1 StartAngle=0 EndAngle=3.14159
    g107: ArcOfCircle CenterX=-45.8 CenterY=-30.2 CenterZ=0 NormalX=0 NormalY=0 NormalZ=1 AngleXU=3.14159 Radius=1 StartAngle=3.14159 EndAngle=6.28319
    g108: LineSegment StartX=-44.8 StartY=-30.2 StartZ=0 EndX=-44.8 EndY=-32.2 EndZ=0
    g109: LineSegment StartX=-46.8 StartY=-32.2 StartZ=0 EndX=-46.8 EndY=-30.2 EndZ=0
    g110: ArcOfCircle CenterX=-49.8 CenterY=-47.2 CenterZ=0 NormalX=0 NormalY=0 NormalZ=1 AngleXU=3.14159 Radius=1 StartAngle=0 EndAngle=3.14159
    g111: ArcOfCircle CenterX=-49.8 CenterY=-45.2 CenterZ=0 NormalX=0 NormalY=0 NormalZ=1 AngleXU=3.14159 Radius=1 StartAngle=3.14159 EndAngle=6.28319
    g112: LineSegment StartX=-48.8 StartY=-45.2 StartZ=0 EndX=-48.8 EndY=-47.2 EndZ=0
    g113: LineSegment StartX=-50.8 StartY=-47.2 StartZ=0 EndX=-50.8 EndY=-45.2 EndZ=0
    g114: Circle CenterX=-49.8 CenterY=-41.2 CenterZ=0 NormalX=0 NormalY=0 NormalZ=-1 AngleXU=-3.14159 Radius=1
    g115: ArcOfCircle CenterX=-49.8 CenterY=-37.2 CenterZ=0 NormalX=0 NormalY=0 NormalZ=1 AngleXU=3.14159 Radius=1 StartAngle=0 EndAngle=3.14159
    g116: ArcOfCircle CenterX=-49.8 CenterY=-35.2 CenterZ=0 NormalX=0 NormalY=0 NormalZ=1 AngleXU=3.14159 Radius=1 StartAngle=3.14159 EndAngle=6.28319
    g117: LineSegment StartX=-48.8 StartY=-35.2 StartZ=0 EndX=-48.8 EndY=-37.2 EndZ=0
    g118: LineSegment StartX=-50.8 StartY=-37.2 StartZ=0 EndX=-50.8 EndY=-35.2 EndZ=0
    g119: Circle CenterX=-49.8 CenterY=-31.2 CenterZ=0 NormalX=0 NormalY=0 NormalZ=-1 AngleXU=-3.14159 Radius=1
FEATURE [PartDesign::Pocket] Pocket025  label="Top_vents"
  BaseFeature = -> Fillet007
  Direction = (0,0,-1)
  Length = 5
  Length2 = 5
  Profile = -> Sketch032
  ReferenceAxis = -> Sketch032 [N_Axis]
  Refine = true
  Suppressed = false
  Type = 1
FEATURE [PartDesign::Body] Body002  label="Top"
  AllowCompound = false
  Group = -> [Sketch011,Pad006,Sketch024,Pad007,Sketch012,Pad008,Sketch013,Pocket015,Sketch015,Pocket016,Sketch016,Pocket017,Sketch017,Pocket018,Sketch018,Pocket019,Sketch019,Pocket020,Sketch020,Pocket021,Sketch022,Pad009,Fillet003,Fillet004,Fillet005,Fillet006,Fillet007,Sketch032,Pocket025]
  Origin = -> Origin003
  Tip = -> Pocket025
FEATURE [App::Part] Part  label="Top_part"
  Group = -> [Body002]
  Origin = -> Origin002
  Placement = pos=(0,0,17.4) rot=(0,0,1;0rad)
  expr: .Placement.Base.z = <<Bottom_base>>.Length + <<Bottom_outer_wall>>.Length
